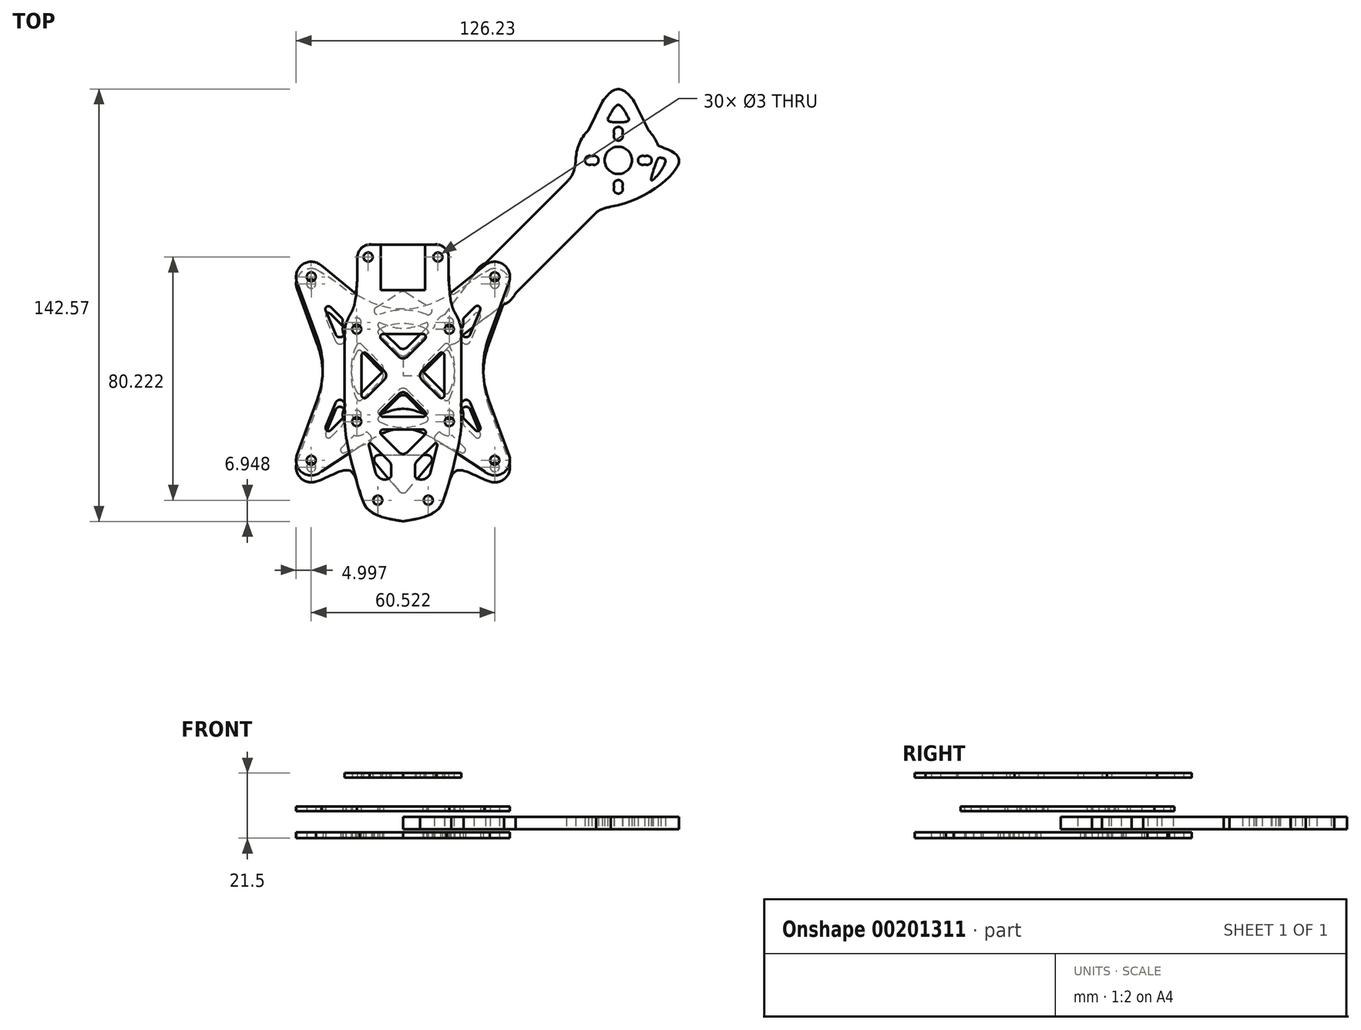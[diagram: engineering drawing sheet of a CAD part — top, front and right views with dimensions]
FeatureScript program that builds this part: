
annotation { "Feature Type Name" : "Feature", "Feature Type Description" : "" }
export const myFeature = defineFeature(function(context is Context, id is Id, definition is map)
    precondition{}
    {
        {
            var Q0;
            Q0=qCreatedBy(makeId("Top.planeOp"),FACE);
            var sketch = newSketch(context, id + "F0", { "sketchPlane" : qUnion([Q0])});
            skLineSegment(sketch, "E0.bottom", {"start": v(-15.25, 15.25) * mm, "end": v(15.25, 15.25) * mm, "construction": true});
            skLineSegment(sketch, "E0.top", {"start": v(-15.25, -15.25) * mm, "end": v(15.25, -15.25) * mm, "construction": true});
            skLineSegment(sketch, "E0.left", {"start": v(-15.25, 15.25) * mm, "end": v(-15.25, -15.25) * mm, "construction": true});
            skLineSegment(sketch, "E0.right", {"start": v(15.25, 15.25) * mm, "end": v(15.25, -15.25) * mm, "construction": true});
            skPoint(sketch, "E0.middle", {"position": v(0, 0) * mm});
            skLineSegment(sketch, "E1.bottom", {"start": v(30.25, 30.25) * mm, "end": v(-30.25, 30.25) * mm, "construction": true});
            skLineSegment(sketch, "E1.top", {"start": v(30.25, -30.25) * mm, "end": v(-30.25, -30.25) * mm, "construction": true});
            skLineSegment(sketch, "E1.left", {"start": v(30.25, 30.25) * mm, "end": v(30.25, -30.25) * mm, "construction": true});
            skLineSegment(sketch, "E1.right", {"start": v(-30.25, 30.25) * mm, "end": v(-30.25, -30.25) * mm, "construction": true});
            skLineSegment(sketch, "E2.bottom", {"start": v(-70.96, 70.96) * mm, "end": v(70.96, 70.96) * mm, "construction": true});
            skLineSegment(sketch, "E2.top", {"start": v(-70.96, -70.96) * mm, "end": v(70.96, -70.96) * mm, "construction": true});
            skLineSegment(sketch, "E2.left", {"start": v(-70.96, 70.96) * mm, "end": v(-70.96, -70.96) * mm, "construction": true});
            skLineSegment(sketch, "E2.right", {"start": v(70.96, 70.96) * mm, "end": v(70.96, -70.96) * mm, "construction": true});
            skCircle(sketch, "E3", {"center": v(70.96, 70.96) * mm, "radius": 8 * mm, "construction": true});
            skCircle(sketch, "E4", {"center": v(70.96, -70.96) * mm, "radius": 8 * mm, "construction": true});
            skCircle(sketch, "E5", {"center": v(-70.96, -70.96) * mm, "radius": 8 * mm, "construction": true});
            skCircle(sketch, "E6", {"center": v(-70.96, 70.96) * mm, "radius": 8 * mm, "construction": true});
            skCircle(sketch, "E7", {"center": v(70.96, 70.96) * mm, "radius": 9.5 * mm, "construction": true});
            skCircle(sketch, "E8", {"center": v(70.96, -70.96) * mm, "radius": 9.5 * mm, "construction": true});
            skCircle(sketch, "E9", {"center": v(-70.96, -70.96) * mm, "radius": 9.5 * mm, "construction": true});
            skCircle(sketch, "E10", {"center": v(-70.96, 70.96) * mm, "radius": 9.5 * mm, "construction": true});
            skCircle(sketch, "E11", {"center": v(70.96, 70.96) * mm, "radius": 14 * mm, "construction": true});
            skCircle(sketch, "E12", {"center": v(-70.96, 70.96) * mm, "radius": 14 * mm, "construction": true});
            skCircle(sketch, "E13", {"center": v(70.96, -70.96) * mm, "radius": 14 * mm, "construction": true});
            skCircle(sketch, "E14", {"center": v(-70.96, -70.96) * mm, "radius": 14 * mm, "construction": true});
            skCircle(sketch, "E15", {"center": v(70.96, 70.96) * mm, "radius": 63.5 * mm, "construction": true});
            skCircle(sketch, "E16", {"center": v(70.96, -70.96) * mm, "radius": 63.5 * mm, "construction": true});
            skCircle(sketch, "E17", {"center": v(-70.96, -70.96) * mm, "radius": 63.5 * mm, "construction": true});
            skCircle(sketch, "E18", {"center": v(-70.96, 70.96) * mm, "radius": 63.5 * mm, "construction": true});
            skLineSegment(sketch, "E19", {"start": v(0, 30.25) * mm, "end": v(0, 37.76) * mm, "construction": true});
            skLineSegment(sketch, "E20", {"start": v(0, 37.76) * mm, "end": v(15, 37.76) * mm, "construction": true});
            skLineSegment(sketch, "E21", {"start": v(0, -30.25) * mm, "end": v(0, -37.76) * mm, "construction": true});
            skLineSegment(sketch, "E22.bottom", {"start": v(-26.17, 26.25) * mm, "end": v(26.21, 26.25) * mm, "construction": true});
            skLineSegment(sketch, "E22.top", {"start": v(-26.21, -26.25) * mm, "end": v(26.17, -26.25) * mm, "construction": true});
            skLineSegment(sketch, "E22.left", {"start": v(-26.17, 26.25) * mm, "end": v(-26.17, -26.13) * mm, "construction": true});
            skLineSegment(sketch, "E22.right", {"start": v(26.21, 26.25) * mm, "end": v(26.21, -26.2) * mm, "construction": true});
            skCircle(sketch, "E23", {"center": v(30.25, 30.25) * mm, "radius": 5 * mm, "construction": true});
            skCircle(sketch, "E24", {"center": v(-30.25, 30.25) * mm, "radius": 5 * mm, "construction": true});
            skCircle(sketch, "E25", {"center": v(30.25, -30.25) * mm, "radius": 5 * mm, "construction": true});
            skCircle(sketch, "E26", {"center": v(-30.25, -30.25) * mm, "radius": 5 * mm, "construction": true});
            skLineSegment(sketch, "E27.bottom", {"start": v(24.5, 24.5) * mm, "end": v(-24.5, 24.5) * mm, "construction": true});
            skLineSegment(sketch, "E27.top", {"start": v(24.5, -24.5) * mm, "end": v(-24.5, -24.5) * mm, "construction": true});
            skLineSegment(sketch, "E27.left", {"start": v(24.5, 24.5) * mm, "end": v(24.5, -24.5) * mm, "construction": true});
            skLineSegment(sketch, "E27.right", {"start": v(-24.5, 24.5) * mm, "end": v(-24.5, -24.5) * mm, "construction": true});
            skLineSegment(sketch, "E28", {"start": v(-26.17, 26.25) * mm, "end": v(-30.25, 30.25) * mm, "construction": true});
            skLineSegment(sketch, "E29", {"start": v(-26.68, 26.75) * mm, "end": v(-33.82, 33.75) * mm, "construction": true});
            skLineSegment(sketch, "E30", {"start": v(-31.8, 31.77) * mm, "end": v(-28.66, 34.99) * mm, "construction": true});
            skLineSegment(sketch, "E31", {"start": v(-31.8, 31.77) * mm, "end": v(-34.96, 28.56) * mm, "construction": true});
            skArc(sketch, "E32", {"start": v(-28.66, 34.99) * mm, "mid": v(-33.82, 33.75) * mm, "end": v(-34.96, 28.56) * mm});
            skLineSegment(sketch, "E33", {"start": v(26.21, 26.25) * mm, "end": v(30.25, 30.25) * mm, "construction": true});
            skLineSegment(sketch, "E34", {"start": v(26.7, 26.73) * mm, "end": v(33.8, 33.77) * mm, "construction": true});
            skLineSegment(sketch, "E35", {"start": v(31.8, 31.78) * mm, "end": v(34.96, 28.58) * mm, "construction": true});
            skLineSegment(sketch, "E36", {"start": v(31.8, 31.78) * mm, "end": v(28.63, 34.98) * mm, "construction": true});
            skArc(sketch, "E37", {"start": v(34.96, 28.58) * mm, "mid": v(33.8, 33.77) * mm, "end": v(28.63, 34.98) * mm});
            skLineSegment(sketch, "E38", {"start": v(26.17, -26.25) * mm, "end": v(30.25, -30.25) * mm, "construction": true});
            skLineSegment(sketch, "E39", {"start": v(26.68, -26.75) * mm, "end": v(33.82, -33.75) * mm, "construction": true});
            skLineSegment(sketch, "E40", {"start": v(31.8, -31.77) * mm, "end": v(34.96, -28.56) * mm, "construction": true});
            skLineSegment(sketch, "E41", {"start": v(31.8, -31.77) * mm, "end": v(28.66, -34.99) * mm, "construction": true});
            skArc(sketch, "E42", {"start": v(28.66, -34.99) * mm, "mid": v(33.82, -33.75) * mm, "end": v(34.96, -28.56) * mm});
            skLineSegment(sketch, "E43", {"start": v(-26.21, -26.25) * mm, "end": v(-30.25, -30.25) * mm, "construction": true});
            skLineSegment(sketch, "E44", {"start": v(-26.7, -26.73) * mm, "end": v(-33.8, -33.77) * mm, "construction": true});
            skLineSegment(sketch, "E45", {"start": v(-31.8, -31.78) * mm, "end": v(-28.63, -34.98) * mm, "construction": true});
            skLineSegment(sketch, "E46", {"start": v(-31.8, -31.78) * mm, "end": v(-34.96, -28.58) * mm, "construction": true});
            skArc(sketch, "E47", {"start": v(-34.96, -28.58) * mm, "mid": v(-33.8, -33.77) * mm, "end": v(-28.63, -34.98) * mm});
            skLineSegment(sketch, "E48", {"start": v(-34.96, -28.58) * mm, "end": v(-28.28, -10.31) * mm});
            skLineSegment(sketch, "E49", {"start": v(-28.28, 10.31) * mm, "end": v(-34.96, 28.56) * mm});
            skLineSegment(sketch, "E50", {"start": v(34.96, 28.58) * mm, "end": v(28.28, 10.31) * mm});
            skLineSegment(sketch, "E51", {"start": v(28.28, -10.31) * mm, "end": v(34.96, -28.56) * mm});
            skPoint(sketch, "E52.visualSharp", {"position": v(24.5, 0) * mm});
            skArc(sketch, "E52.filletArc", {"start": v(28.28, 10.31) * mm, "mid": v(26.45, 0) * mm, "end": v(28.28, -10.31) * mm});
            skPoint(sketch, "E53.visualSharp", {"position": v(-24.5, 0) * mm});
            skArc(sketch, "E53.filletArc", {"start": v(-28.28, -10.31) * mm, "mid": v(-26.45, 0) * mm, "end": v(-28.28, 10.31) * mm});
            skFitSpline(sketch, "E54", {"points": [v(-28.66, 34.99) * mm, v(-15, 37.76) * mm], "startDerivative": vector(40.9, -21.49) * mm, "endDerivative": vector(0.75, 54.16) * mm});
            skFitSpline(sketch, "E55", {"points": [v(15, 37.76) * mm, v(28.63, 34.98) * mm], "startDerivative": vector(0.75, -54.16) * mm, "endDerivative": vector(40.9, 21.46) * mm});
            skLineSegment(sketch, "E56", {"start": v(-15.25, 19.7) * mm, "end": v(15.25, 19.7) * mm, "construction": true});
            skPoint(sketch, "E57.endSnap0", {"position": v(0, -15.25) * mm});
            skLineSegment(sketch, "E58", {"start": v(-15.25, -19.7) * mm, "end": v(15.25, -19.7) * mm, "construction": true});
            skLineSegment(sketch, "E59", {"start": v(-14.33, -37.76) * mm, "end": v(14.33, -37.76) * mm, "construction": true});
            skCircle(sketch, "E60", {"center": v(-30.25, 30.25) * mm, "radius": 1.5 * mm});
            skCircle(sketch, "E61", {"center": v(30.25, 30.25) * mm, "radius": 1.5 * mm});
            skCircle(sketch, "E62", {"center": v(15.25, 15.25) * mm, "radius": 1.5 * mm});
            skCircle(sketch, "E63", {"center": v(-15.25, 15.25) * mm, "radius": 1.5 * mm});
            skCircle(sketch, "E64", {"center": v(-15.25, -15.25) * mm, "radius": 1.5 * mm});
            skCircle(sketch, "E65", {"center": v(15.25, -15.25) * mm, "radius": 1.5 * mm});
            skCircle(sketch, "E66", {"center": v(30.25, -30.25) * mm, "radius": 1.5 * mm});
            skCircle(sketch, "E67", {"center": v(-30.25, -30.25) * mm, "radius": 1.5 * mm});
            skCircle(sketch, "E68", {"center": v(-11.5, 39.06) * mm, "radius": 1.5 * mm});
            skCircle(sketch, "E69", {"center": v(11.5, 39.06) * mm, "radius": 1.5 * mm});
            skLineSegment(sketch, "E70", {"start": v(0, 37.76) * mm, "end": v(0, 15.25) * mm, "construction": true});
            skLineSegment(sketch, "E71", {"start": v(0, -44.58) * mm, "end": v(-11, -44.58) * mm, "construction": true});
            skLineSegment(sketch, "E72", {"start": v(0, -44.58) * mm, "end": v(11, -44.58) * mm, "construction": true});
            skPoint(sketch, "E73.visualSharp", {"position": v(-14.33, -37.76) * mm});
            skPoint(sketch, "E74.visualSharp", {"position": v(14.33, -37.76) * mm});
            skCircle(sketch, "E75", {"center": v(0, 0) * mm, "radius": 17.11 * mm, "construction": true});
            skLineSegment(sketch, "E76", {"start": v(0, 0) * mm, "end": v(14.1, 14.1) * mm, "construction": true});
            skLineSegment(sketch, "E77", {"start": v(0, 0) * mm, "end": v(-15.25, 15.25) * mm, "construction": true});
            skLineSegment(sketch, "E78", {"start": v(0, 0) * mm, "end": v(-15.32, -15.32) * mm, "construction": true});
            skLineSegment(sketch, "E79", {"start": v(0, 0) * mm, "end": v(15.25, -15.25) * mm, "construction": true});
            skLineSegment(sketch, "E80", {"start": v(-10.7, 10.7) * mm, "end": v(-7.86, 13.52) * mm, "construction": true});
            skLineSegment(sketch, "E81", {"start": v(-10.7, 10.7) * mm, "end": v(-13.52, 7.86) * mm, "construction": true});
            skLineSegment(sketch, "E82", {"start": v(9.03, 9.03) * mm, "end": v(11.86, 6.2) * mm, "construction": true});
            skLineSegment(sketch, "E83", {"start": v(9.03, 9.03) * mm, "end": v(6.2, 11.86) * mm, "construction": true});
            skLineSegment(sketch, "E84", {"start": v(9.8, -9.8) * mm, "end": v(12.64, -6.98) * mm, "construction": true});
            skLineSegment(sketch, "E85", {"start": v(9.8, -9.8) * mm, "end": v(6.98, -12.64) * mm, "construction": true});
            skLineSegment(sketch, "E86", {"start": v(-9.52, -9.52) * mm, "end": v(-6.7, -12.35) * mm, "construction": true});
            skLineSegment(sketch, "E87", {"start": v(-9.52, -9.52) * mm, "end": v(-12.35, -6.7) * mm, "construction": true});
            skLineSegment(sketch, "E88.bottom", {"start": v(6.35, 6.35) * mm, "end": v(-6.35, 6.35) * mm, "construction": true});
            skLineSegment(sketch, "E88.top", {"start": v(6.35, -6.35) * mm, "end": v(-6.35, -6.35) * mm, "construction": true});
            skLineSegment(sketch, "E88.left", {"start": v(6.35, 6.35) * mm, "end": v(6.35, -6.35) * mm, "construction": true});
            skLineSegment(sketch, "E88.right", {"start": v(-6.35, 6.35) * mm, "end": v(-6.35, -6.35) * mm, "construction": true});
            skLineSegment(sketch, "E89", {"start": v(6.2, 11.86) * mm, "end": v(8.94, 14.6) * mm, "construction": true});
            skLineSegment(sketch, "E90", {"start": v(11.86, 6.2) * mm, "end": v(14.6, 8.94) * mm, "construction": true});
            skLineSegment(sketch, "E91", {"start": v(8, 13.66) * mm, "end": v(1.41, 7.07) * mm});
            skLineSegment(sketch, "E92", {"start": v(-1.41, 7.07) * mm, "end": v(-8, 13.66) * mm});
            skLineSegment(sketch, "E93", {"start": v(-13.52, 7.86) * mm, "end": v(-14.6, 8.94) * mm, "construction": true});
            skLineSegment(sketch, "E94", {"start": v(-6.7, -12.35) * mm, "end": v(-8.94, -14.6) * mm, "construction": true});
            skLineSegment(sketch, "E95", {"start": v(-8, -13.66) * mm, "end": v(-1.41, -7.07) * mm});
            skLineSegment(sketch, "E96", {"start": v(1.41, -7.07) * mm, "end": v(8, -13.66) * mm});
            skLineSegment(sketch, "E97", {"start": v(13.66, 8) * mm, "end": v(7.07, 1.41) * mm});
            skLineSegment(sketch, "E98", {"start": v(7.07, -1.41) * mm, "end": v(13.66, -8) * mm});
            skPoint(sketch, "E99", {"position": v(-7.77, 15.25) * mm});
            skPoint(sketch, "E100", {"position": v(7.77, 15.25) * mm});
            skPoint(sketch, "E101", {"position": v(15.25, 7.77) * mm});
            skPoint(sketch, "E102", {"position": v(15.25, -7.77) * mm});
            skPoint(sketch, "E103", {"position": v(7.77, -15.25) * mm});
            skPoint(sketch, "E104", {"position": v(-7.77, -15.25) * mm});
            skPoint(sketch, "E105", {"position": v(-15.25, -7.77) * mm});
            skPoint(sketch, "E106", {"position": v(-15.25, 7.77) * mm});
            skLineSegment(sketch, "E107", {"start": v(-7.79, 15.24) * mm, "end": v(-7.77, 15.25) * mm});
            skLineSegment(sketch, "E108", {"start": v(7.79, 15.24) * mm, "end": v(7.77, 15.25) * mm});
            skLineSegment(sketch, "E109", {"start": v(15.24, 7.79) * mm, "end": v(15.25, 7.77) * mm});
            skLineSegment(sketch, "E110", {"start": v(15.24, -7.79) * mm, "end": v(15.25, -7.77) * mm});
            skLineSegment(sketch, "E111", {"start": v(7.79, -15.24) * mm, "end": v(7.77, -15.25) * mm});
            skLineSegment(sketch, "E112", {"start": v(-7.77, -15.25) * mm, "end": v(-7.79, -15.24) * mm});
            skLineSegment(sketch, "E113", {"start": v(-15.24, -7.79) * mm, "end": v(-15.25, -7.77) * mm});
            skLineSegment(sketch, "E114", {"start": v(-15.24, 7.79) * mm, "end": v(-15.25, 7.77) * mm});
            skPoint(sketch, "E115", {"position": v(0, 17.11) * mm});
            skPoint(sketch, "E116", {"position": v(17.11, 0) * mm});
            skPoint(sketch, "E117", {"position": v(-17.11, 0) * mm});
            skPoint(sketch, "E118", {"position": v(0, -17.11) * mm});
            skArc(sketch, "E119", {"start": v(7.77, 15.25) * mm, "mid": v(0, 17.11) * mm, "end": v(-7.77, 15.25) * mm});
            skArc(sketch, "E120", {"start": v(15.25, -7.77) * mm, "mid": v(17.11, 0) * mm, "end": v(15.25, 7.77) * mm});
            skArc(sketch, "E121", {"start": v(-7.77, -15.25) * mm, "mid": v(0, -17.11) * mm, "end": v(7.77, -15.25) * mm});
            skArc(sketch, "E122", {"start": v(-15.25, 7.77) * mm, "mid": v(-17.11, 0) * mm, "end": v(-15.25, -7.77) * mm});
            skPoint(sketch, "E123.visualSharp", {"position": v(-5.66, 0) * mm});
            skPoint(sketch, "E124.visualSharp", {"position": v(-14.6, 8.94) * mm});
            skArc(sketch, "E124.filletArc", {"start": v(-13.66, 8) * mm, "mid": v(-14.5, 8.29) * mm, "end": v(-15.24, 7.79) * mm});
            skPoint(sketch, "E125.visualSharp", {"position": v(-14.6, -8.94) * mm});
            skArc(sketch, "E125.filletArc", {"start": v(-15.24, -7.79) * mm, "mid": v(-14.5, -8.29) * mm, "end": v(-13.66, -8) * mm});
            skPoint(sketch, "E126.visualSharp", {"position": v(-8.94, 14.6) * mm});
            skArc(sketch, "E126.filletArc", {"start": v(-7.79, 15.24) * mm, "mid": v(-8.29, 14.5) * mm, "end": v(-8, 13.66) * mm});
            skPoint(sketch, "E127.visualSharp", {"position": v(8.94, 14.6) * mm});
            skArc(sketch, "E127.filletArc", {"start": v(8, 13.66) * mm, "mid": v(8.29, 14.5) * mm, "end": v(7.79, 15.24) * mm});
            skPoint(sketch, "E128.visualSharp", {"position": v(14.6, -8.94) * mm});
            skArc(sketch, "E128.filletArc", {"start": v(13.66, -8) * mm, "mid": v(14.5, -8.29) * mm, "end": v(15.24, -7.79) * mm});
            skPoint(sketch, "E129.visualSharp", {"position": v(14.6, 8.94) * mm});
            skArc(sketch, "E129.filletArc", {"start": v(15.24, 7.79) * mm, "mid": v(14.5, 8.29) * mm, "end": v(13.66, 8) * mm});
            skPoint(sketch, "E130.visualSharp", {"position": v(8.94, -14.6) * mm});
            skArc(sketch, "E130.filletArc", {"start": v(7.79, -15.24) * mm, "mid": v(8.29, -14.5) * mm, "end": v(8, -13.66) * mm});
            skPoint(sketch, "E131.visualSharp", {"position": v(-8.94, -14.6) * mm});
            skArc(sketch, "E131.filletArc", {"start": v(-8, -13.66) * mm, "mid": v(-8.29, -14.5) * mm, "end": v(-7.79, -15.24) * mm});
            skLineSegment(sketch, "E132", {"start": v(-13.66, 8) * mm, "end": v(-7.07, 1.41) * mm});
            skLineSegment(sketch, "E133", {"start": v(-13.66, -8) * mm, "end": v(-7.07, -1.41) * mm});
            skArc(sketch, "E134.filletArc", {"start": v(-7.07, -1.41) * mm, "mid": v(-6.49, 0) * mm, "end": v(-7.07, 1.41) * mm});
            skPoint(sketch, "E135.visualSharp", {"position": v(0, -5.66) * mm});
            skArc(sketch, "E135.filletArc", {"start": v(1.41, -7.07) * mm, "mid": v(0, -6.49) * mm, "end": v(-1.41, -7.07) * mm});
            skPoint(sketch, "E136.visualSharp", {"position": v(5.66, 0) * mm});
            skArc(sketch, "E136.filletArc", {"start": v(7.07, 1.41) * mm, "mid": v(6.49, 0) * mm, "end": v(7.07, -1.41) * mm});
            skPoint(sketch, "E137.visualSharp", {"position": v(0, 5.66) * mm});
            skArc(sketch, "E137.filletArc", {"start": v(-1.41, 7.07) * mm, "mid": v(0, 6.49) * mm, "end": v(1.41, 7.07) * mm});
            skLineSegment(sketch, "E138", {"start": v(-12.9, 12.9) * mm, "end": v(-11.14, 14.67) * mm, "construction": true});
            skLineSegment(sketch, "E139", {"start": v(-12.9, 12.9) * mm, "end": v(-14.67, 11.14) * mm, "construction": true});
            skLineSegment(sketch, "E140", {"start": v(-14.67, 11.14) * mm, "end": v(-27.4, 23.87) * mm, "construction": true});
            skPoint(sketch, "E141", {"position": v(-17.57, 14.03) * mm});
            skCircle(sketch, "E142", {"center": v(-15.25, 15.25) * mm, "radius": 4.62 * mm, "construction": true});
            skLineSegment(sketch, "E143", {"start": v(-27.4, 23.87) * mm, "end": v(-21.1, 8.64) * mm, "construction": true});
            skLineSegment(sketch, "E144", {"start": v(-15.25, 15.25) * mm, "end": v(-21.32, 9.18) * mm, "construction": true});
            skLineSegment(sketch, "E145", {"start": v(-18.86, 11.64) * mm, "end": v(-19.74, 10.76) * mm});
            skLineSegment(sketch, "E146", {"start": v(-22.18, 11.25) * mm, "end": v(-25.48, 19.23) * mm});
            skLineSegment(sketch, "E147", {"start": v(-23.85, 20.32) * mm, "end": v(-20.04, 16.5) * mm});
            skLineSegment(sketch, "E148", {"start": v(-19.83, 15.85) * mm, "end": v(-19.85, 15.74) * mm});
            skLineSegment(sketch, "E149", {"start": v(-18.84, 12.33) * mm, "end": v(-18.85, 12.35) * mm});
            skPoint(sketch, "E150", {"position": v(-19.67, 13.9) * mm});
            skArc(sketch, "E151", {"start": v(-19.85, 15.74) * mm, "mid": v(-19.69, 13.95) * mm, "end": v(-18.85, 12.35) * mm});
            skPoint(sketch, "E152.visualSharp", {"position": v(-27.4, 23.87) * mm});
            skArc(sketch, "E152.filletArc", {"start": v(-23.85, 20.32) * mm, "mid": v(-25.11, 20.44) * mm, "end": v(-25.48, 19.23) * mm});
            skPoint(sketch, "E153.visualSharp", {"position": v(-21.32, 9.18) * mm});
            skArc(sketch, "E153.filletArc", {"start": v(-22.18, 11.25) * mm, "mid": v(-21.1, 10.35) * mm, "end": v(-19.74, 10.76) * mm});
            skPoint(sketch, "E154.visualSharp", {"position": v(-18.52, 11.98) * mm});
            skArc(sketch, "E154.filletArc", {"start": v(-18.86, 11.64) * mm, "mid": v(-18.7, 11.98) * mm, "end": v(-18.84, 12.33) * mm});
            skPoint(sketch, "E155.visualSharp", {"position": v(-19.77, 16.23) * mm});
            skArc(sketch, "E155.filletArc", {"start": v(-19.83, 15.85) * mm, "mid": v(-19.86, 16.2) * mm, "end": v(-20.04, 16.5) * mm});
            skCircle(sketch, "E156", {"center": v(15.23, 15.26) * mm, "radius": 4.62 * mm, "construction": true});
            skLineSegment(sketch, "E157", {"start": v(15.23, 15.26) * mm, "end": v(12.9, 12.9) * mm, "construction": true});
            skLineSegment(sketch, "E158", {"start": v(12.9, 12.9) * mm, "end": v(14.68, 11.15) * mm, "construction": true});
            skLineSegment(sketch, "E159", {"start": v(12.9, 12.9) * mm, "end": v(11.12, 14.66) * mm, "construction": true});
            skLineSegment(sketch, "E160", {"start": v(11.12, 14.66) * mm, "end": v(23.85, 27.39) * mm, "construction": true});
            skLineSegment(sketch, "E161", {"start": v(14.68, 11.15) * mm, "end": v(27.32, 23.97) * mm, "construction": true});
            skLineSegment(sketch, "E162", {"start": v(15.25, 15.25) * mm, "end": v(21.37, 9.22) * mm, "construction": true});
            skLineSegment(sketch, "E163", {"start": v(21.37, 9.22) * mm, "end": v(27.32, 23.97) * mm, "construction": true});
            skLineSegment(sketch, "E164", {"start": v(19.8, 15.9) * mm, "end": v(19.82, 15.79) * mm});
            skLineSegment(sketch, "E165", {"start": v(18.84, 12.37) * mm, "end": v(18.86, 12.4) * mm});
            skLineSegment(sketch, "E166", {"start": v(20.01, 16.55) * mm, "end": v(23.8, 20.4) * mm});
            skLineSegment(sketch, "E167", {"start": v(25.45, 19.33) * mm, "end": v(22.2, 11.3) * mm});
            skLineSegment(sketch, "E168", {"start": v(19.77, 10.8) * mm, "end": v(18.86, 11.69) * mm});
            skPoint(sketch, "E169", {"position": v(19.65, 13.92) * mm});
            skArc(sketch, "E170", {"start": v(18.86, 12.4) * mm, "mid": v(19.68, 14) * mm, "end": v(19.82, 15.79) * mm});
            skPoint(sketch, "E171.visualSharp", {"position": v(18.53, 12.02) * mm});
            skArc(sketch, "E171.filletArc", {"start": v(18.84, 12.37) * mm, "mid": v(18.72, 12.03) * mm, "end": v(18.86, 11.69) * mm});
            skPoint(sketch, "E172.visualSharp", {"position": v(19.74, 16.28) * mm});
            skArc(sketch, "E172.filletArc", {"start": v(20.01, 16.55) * mm, "mid": v(19.83, 16.25) * mm, "end": v(19.8, 15.9) * mm});
            skPoint(sketch, "E173.visualSharp", {"position": v(27.32, 23.97) * mm});
            skArc(sketch, "E173.filletArc", {"start": v(25.45, 19.33) * mm, "mid": v(25.07, 20.54) * mm, "end": v(23.8, 20.4) * mm});
            skPoint(sketch, "E174.visualSharp", {"position": v(21.37, 9.22) * mm});
            skArc(sketch, "E174.filletArc", {"start": v(19.77, 10.8) * mm, "mid": v(21.12, 10.4) * mm, "end": v(22.2, 11.3) * mm});
            skCircle(sketch, "E175", {"center": v(-15.25, -15.25) * mm, "radius": 4.62 * mm, "construction": true});
            skCircle(sketch, "E176", {"center": v(15.25, -15.25) * mm, "radius": 4.62 * mm, "construction": true});
            skLineSegment(sketch, "E177", {"start": v(-15.25, -15.25) * mm, "end": v(-12.9, -12.9) * mm, "construction": true});
            skLineSegment(sketch, "E178", {"start": v(-12.9, -12.9) * mm, "end": v(-11.14, -14.67) * mm, "construction": true});
            skLineSegment(sketch, "E179", {"start": v(-12.9, -12.9) * mm, "end": v(-14.67, -11.14) * mm, "construction": true});
            skLineSegment(sketch, "E180", {"start": v(-11.14, -14.67) * mm, "end": v(-23.87, -27.4) * mm, "construction": true});
            skLineSegment(sketch, "E181", {"start": v(-14.67, -11.14) * mm, "end": v(-27.4, -23.87) * mm, "construction": true});
            skLineSegment(sketch, "E182", {"start": v(-15.25, -15.25) * mm, "end": v(-9.18, -21.32) * mm, "construction": true});
            skLineSegment(sketch, "E183", {"start": v(-15.25, -15.25) * mm, "end": v(-21.32, -9.18) * mm, "construction": true});
            skLineSegment(sketch, "E184", {"start": v(-25.48, -19.23) * mm, "end": v(-22.18, -11.25) * mm});
            skLineSegment(sketch, "E185", {"start": v(-19.74, -10.76) * mm, "end": v(-18.86, -11.64) * mm});
            skLineSegment(sketch, "E186", {"start": v(-23.85, -20.32) * mm, "end": v(-20.04, -16.5) * mm});
            skLineSegment(sketch, "E187", {"start": v(-18.84, -12.33) * mm, "end": v(-18.85, -12.35) * mm});
            skLineSegment(sketch, "E188", {"start": v(-19.83, -15.85) * mm, "end": v(-19.85, -15.74) * mm});
            skPoint(sketch, "E189", {"position": v(-19.69, -13.94) * mm});
            skArc(sketch, "E190", {"start": v(-18.85, -12.35) * mm, "mid": v(-19.69, -13.95) * mm, "end": v(-19.85, -15.74) * mm});
            skPoint(sketch, "E191.visualSharp", {"position": v(-18.52, -11.98) * mm});
            skArc(sketch, "E191.filletArc", {"start": v(-18.84, -12.33) * mm, "mid": v(-18.7, -11.98) * mm, "end": v(-18.86, -11.64) * mm});
            skPoint(sketch, "E192.visualSharp", {"position": v(-19.77, -16.23) * mm});
            skArc(sketch, "E192.filletArc", {"start": v(-20.04, -16.5) * mm, "mid": v(-19.86, -16.2) * mm, "end": v(-19.83, -15.85) * mm});
            skPoint(sketch, "E193.visualSharp", {"position": v(-27.4, -23.87) * mm});
            skArc(sketch, "E193.filletArc", {"start": v(-25.48, -19.23) * mm, "mid": v(-25.11, -20.44) * mm, "end": v(-23.85, -20.32) * mm});
            skPoint(sketch, "E194.visualSharp", {"position": v(-21.32, -9.18) * mm});
            skArc(sketch, "E194.filletArc", {"start": v(-19.74, -10.76) * mm, "mid": v(-21.1, -10.35) * mm, "end": v(-22.18, -11.25) * mm});
            skLineSegment(sketch, "E195", {"start": v(15.25, -15.25) * mm, "end": v(12.9, -12.9) * mm, "construction": true});
            skLineSegment(sketch, "E196", {"start": v(12.9, -12.9) * mm, "end": v(14.67, -11.14) * mm, "construction": true});
            skLineSegment(sketch, "E197", {"start": v(12.9, -12.9) * mm, "end": v(11.14, -14.67) * mm, "construction": true});
            skLineSegment(sketch, "E198", {"start": v(14.67, -11.14) * mm, "end": v(27.4, -23.87) * mm, "construction": true});
            skLineSegment(sketch, "E199", {"start": v(15.25, -15.25) * mm, "end": v(21.32, -9.18) * mm, "construction": true});
            skLineSegment(sketch, "E200", {"start": v(22.18, -11.25) * mm, "end": v(25.48, -19.23) * mm});
            skLineSegment(sketch, "E201", {"start": v(23.85, -20.32) * mm, "end": v(20.04, -16.5) * mm});
            skLineSegment(sketch, "E202", {"start": v(19.74, -10.76) * mm, "end": v(18.86, -11.64) * mm});
            skLineSegment(sketch, "E203", {"start": v(18.84, -12.33) * mm, "end": v(18.85, -12.35) * mm});
            skLineSegment(sketch, "E204", {"start": v(19.83, -15.85) * mm, "end": v(19.85, -15.74) * mm});
            skPoint(sketch, "E205", {"position": v(19.64, -13.8) * mm});
            skArc(sketch, "E206", {"start": v(19.85, -15.74) * mm, "mid": v(19.69, -13.95) * mm, "end": v(18.85, -12.35) * mm});
            skPoint(sketch, "E207.visualSharp", {"position": v(21.32, -9.18) * mm});
            skArc(sketch, "E207.filletArc", {"start": v(22.18, -11.25) * mm, "mid": v(21.1, -10.35) * mm, "end": v(19.74, -10.76) * mm});
            skPoint(sketch, "E208.visualSharp", {"position": v(19.77, -16.23) * mm});
            skArc(sketch, "E208.filletArc", {"start": v(19.83, -15.85) * mm, "mid": v(19.86, -16.2) * mm, "end": v(20.04, -16.5) * mm});
            skPoint(sketch, "E209.visualSharp", {"position": v(18.52, -11.98) * mm});
            skArc(sketch, "E209.filletArc", {"start": v(18.86, -11.64) * mm, "mid": v(18.7, -11.98) * mm, "end": v(18.84, -12.33) * mm});
            skPoint(sketch, "E210.visualSharp", {"position": v(27.4, -23.87) * mm});
            skArc(sketch, "E210.filletArc", {"start": v(23.85, -20.32) * mm, "mid": v(25.11, -20.44) * mm, "end": v(25.48, -19.23) * mm});
            skPoint(sketch, "E211", {"position": v(0, -48.1) * mm});
            skLineSegment(sketch, "E212", {"start": v(0, -31.42) * mm, "end": v(17.54, -31.42) * mm, "construction": true});
            skLineSegment(sketch, "E213", {"start": v(0, -31.42) * mm, "end": v(-17.54, -31.42) * mm, "construction": true});
            skFitSpline(sketch, "E214", {"points": [v(28.66, -34.99) * mm, v(17.54, -31.42) * mm, v(14.33, -37.76) * mm], "startDerivative": vector(-22.15, 6.9) * mm, "endDerivative": vector(-5.52, -13.66) * mm});
            skFitSpline(sketch, "E215", {"points": [v(14.33, -37.76) * mm, v(11, -44.58) * mm, v(0, -48.1) * mm], "startDerivative": vector(-4.65, -17.21) * mm, "endDerivative": vector(-23.36, -3.95) * mm});
            skFitSpline(sketch, "E216", {"points": [v(-28.63, -34.98) * mm, v(-17.54, -31.42) * mm, v(-14.33, -37.76) * mm], "startDerivative": vector(22.11, 6.89) * mm, "endDerivative": vector(5.52, -13.65) * mm});
            skFitSpline(sketch, "E217", {"points": [v(-14.33, -37.76) * mm, v(-11, -44.58) * mm, v(0, -48.1) * mm], "startDerivative": vector(4.65, -17.21) * mm, "endDerivative": vector(23.36, -3.95) * mm});
            skLineSegment(sketch, "E218", {"start": v(-19.23, -25.48) * mm, "end": v(-11.25, -22.18) * mm});
            skLineSegment(sketch, "E219", {"start": v(-10.76, -19.74) * mm, "end": v(-11.64, -18.86) * mm});
            skLineSegment(sketch, "E220", {"start": v(-12.33, -18.84) * mm, "end": v(-12.35, -18.85) * mm});
            skLineSegment(sketch, "E221", {"start": v(-20.32, -23.85) * mm, "end": v(-16.5, -20.04) * mm});
            skLineSegment(sketch, "E222", {"start": v(-15.85, -19.83) * mm, "end": v(-15.74, -19.85) * mm});
            skPoint(sketch, "E223.visualSharp", {"position": v(-9.18, -21.32) * mm});
            skArc(sketch, "E223.filletArc", {"start": v(-11.25, -22.18) * mm, "mid": v(-10.35, -21.1) * mm, "end": v(-10.76, -19.74) * mm});
            skPoint(sketch, "E224.visualSharp", {"position": v(-11.98, -18.52) * mm});
            skArc(sketch, "E224.filletArc", {"start": v(-11.64, -18.86) * mm, "mid": v(-11.98, -18.7) * mm, "end": v(-12.33, -18.84) * mm});
            skPoint(sketch, "E225.visualSharp", {"position": v(-16.23, -19.77) * mm});
            skArc(sketch, "E225.filletArc", {"start": v(-15.85, -19.83) * mm, "mid": v(-16.2, -19.86) * mm, "end": v(-16.5, -20.04) * mm});
            skPoint(sketch, "E226.visualSharp", {"position": v(-23.87, -27.4) * mm});
            skArc(sketch, "E226.filletArc", {"start": v(-20.32, -23.85) * mm, "mid": v(-20.44, -25.11) * mm, "end": v(-19.23, -25.48) * mm});
            skLineSegment(sketch, "E227", {"start": v(15.25, -15.25) * mm, "end": v(9.18, -21.32) * mm, "construction": true});
            skLineSegment(sketch, "E228", {"start": v(11.14, -14.67) * mm, "end": v(23.87, -27.4) * mm, "construction": true});
            skLineSegment(sketch, "E229", {"start": v(19.23, -25.48) * mm, "end": v(11.25, -22.18) * mm});
            skLineSegment(sketch, "E230", {"start": v(10.76, -19.74) * mm, "end": v(11.64, -18.86) * mm});
            skLineSegment(sketch, "E231", {"start": v(12.33, -18.84) * mm, "end": v(12.35, -18.85) * mm});
            skLineSegment(sketch, "E232", {"start": v(20.32, -23.85) * mm, "end": v(16.5, -20.04) * mm});
            skLineSegment(sketch, "E233", {"start": v(15.85, -19.83) * mm, "end": v(15.74, -19.85) * mm});
            skPoint(sketch, "E234", {"position": v(13.76, -19.63) * mm});
            skArc(sketch, "E235", {"start": v(12.35, -18.85) * mm, "mid": v(13.95, -19.69) * mm, "end": v(15.74, -19.85) * mm});
            skPoint(sketch, "E236.visualSharp", {"position": v(9.18, -21.32) * mm});
            skArc(sketch, "E236.filletArc", {"start": v(10.76, -19.74) * mm, "mid": v(10.35, -21.1) * mm, "end": v(11.25, -22.18) * mm});
            skPoint(sketch, "E237.visualSharp", {"position": v(11.98, -18.52) * mm});
            skArc(sketch, "E237.filletArc", {"start": v(12.33, -18.84) * mm, "mid": v(11.98, -18.7) * mm, "end": v(11.64, -18.86) * mm});
            skPoint(sketch, "E238.visualSharp", {"position": v(23.87, -27.4) * mm});
            skArc(sketch, "E238.filletArc", {"start": v(19.23, -25.48) * mm, "mid": v(20.44, -25.11) * mm, "end": v(20.32, -23.85) * mm});
            skPoint(sketch, "E239.visualSharp", {"position": v(16.23, -19.77) * mm});
            skArc(sketch, "E239.filletArc", {"start": v(16.5, -20.04) * mm, "mid": v(16.2, -19.86) * mm, "end": v(15.85, -19.83) * mm});
            skPoint(sketch, "E240", {"position": v(-14.29, -19.77) * mm});
            skArc(sketch, "E241", {"start": v(-15.74, -19.85) * mm, "mid": v(-13.95, -19.69) * mm, "end": v(-12.35, -18.85) * mm});
            skLineSegment(sketch, "E242", {"start": v(-13.27, -41.16) * mm, "end": v(-8.27, -41.16) * mm, "construction": true});
            skLineSegment(sketch, "E243", {"start": v(-8.27, -41.16) * mm, "end": v(-8.27, -46.16) * mm, "construction": true});
            skLineSegment(sketch, "E244", {"start": v(13.27, -41.16) * mm, "end": v(8.27, -41.16) * mm, "construction": true});
            skLineSegment(sketch, "E245", {"start": v(8.27, -41.16) * mm, "end": v(8.27, -46.16) * mm, "construction": true});
            skCircle(sketch, "E246", {"center": v(8.27, -41.16) * mm, "radius": 1.5 * mm});
            skCircle(sketch, "E247", {"center": v(-8.27, -41.16) * mm, "radius": 1.5 * mm});
            skLineSegment(sketch, "E248", {"start": v(-8.94, 14.6) * mm, "end": v(-8.94, 19.63) * mm, "construction": true});
            skLineSegment(sketch, "E249", {"start": v(8.94, 14.6) * mm, "end": v(8.94, 19.63) * mm, "construction": true});
            skPoint(sketch, "E250", {"position": v(0, 21.57) * mm});
            skLineSegment(sketch, "E251", {"start": v(-7.77, 15.25) * mm, "end": v(-7.77, 20.12) * mm, "construction": true});
            skLineSegment(sketch, "E252", {"start": v(7.79, 15.24) * mm, "end": v(7.79, 20.11) * mm, "construction": true});
            skLineSegment(sketch, "E253", {"start": v(-8.94, 19.63) * mm, "end": v(-8.94, 22.43) * mm, "construction": true});
            skLineSegment(sketch, "E254", {"start": v(8.94, 19.63) * mm, "end": v(8.94, 22.43) * mm, "construction": true});
            skLineSegment(sketch, "E255", {"start": v(-8.94, 22.43) * mm, "end": v(-1.06, 27.36) * mm});
            skLineSegment(sketch, "E256", {"start": v(1.06, 27.36) * mm, "end": v(8.94, 22.43) * mm});
            skArc(sketch, "E257", {"start": v(-8.94, 22.43) * mm, "mid": v(-9.4, 20.74) * mm, "end": v(-7.77, 20.12) * mm});
            skArc(sketch, "E258", {"start": v(7.79, 20.11) * mm, "mid": v(9.41, 20.75) * mm, "end": v(8.94, 22.43) * mm});
            skPoint(sketch, "E259.visualSharp", {"position": v(0, 28.02) * mm});
            skArc(sketch, "E259.filletArc", {"start": v(1.06, 27.36) * mm, "mid": v(0, 27.66) * mm, "end": v(-1.06, 27.36) * mm});
            skArc(sketch, "E260", {"start": v(7.79, 20.11) * mm, "mid": v(0, 21.57) * mm, "end": v(-7.77, 20.12) * mm});
            skLineSegment(sketch, "E261", {"start": v(-8.94, -14.6) * mm, "end": v(-8.94, -19.63) * mm, "construction": true});
            skLineSegment(sketch, "E262", {"start": v(-7.77, -15.25) * mm, "end": v(-7.77, -20.12) * mm, "construction": true});
            skLineSegment(sketch, "E263", {"start": v(7.79, -15.24) * mm, "end": v(7.79, -20.11) * mm, "construction": true});
            skLineSegment(sketch, "E264", {"start": v(8.94, -14.6) * mm, "end": v(8.94, -19.63) * mm, "construction": true});
            skLineSegment(sketch, "E265", {"start": v(-8.94, -19.63) * mm, "end": v(-8.94, -22.43) * mm, "construction": true});
            skLineSegment(sketch, "E266", {"start": v(8.94, -19.63) * mm, "end": v(8.94, -22.43) * mm, "construction": true});
            skPoint(sketch, "E267", {"position": v(0, -26.25) * mm});
            skPoint(sketch, "E268.visualSharp", {"position": v(0, -30.25) * mm});
            skPoint(sketch, "E269", {"position": v(0, -24.5) * mm});
            skLineSegment(sketch, "E270", {"start": v(0, -26.25) * mm, "end": v(-11.25, -26.25) * mm, "construction": true});
            skLineSegment(sketch, "E271", {"start": v(0, -26.25) * mm, "end": v(11.25, -26.25) * mm, "construction": true});
            skPoint(sketch, "E272.visualSharp", {"position": v(-11.25, -26.25) * mm});
            skPoint(sketch, "E273.visualSharp", {"position": v(11.25, -26.25) * mm});
            skPoint(sketch, "E274.visualSharp", {"position": v(0, -37.76) * mm});
            skPoint(sketch, "E275", {"position": v(0, -39.7) * mm});
            skLineSegment(sketch, "E276", {"start": v(-9.19, -28.72) * mm, "end": v(-1.34, -38.1) * mm});
            skLineSegment(sketch, "E277", {"start": v(1.34, -38.1) * mm, "end": v(9.19, -28.72) * mm});
            skLineSegment(sketch, "E278", {"start": v(-8.04, -26.25) * mm, "end": v(8.04, -26.25) * mm});
            skArc(sketch, "E279.filletArc", {"start": v(-8.04, -26.25) * mm, "mid": v(-9.4, -27.12) * mm, "end": v(-9.19, -28.72) * mm});
            skArc(sketch, "E280.filletArc", {"start": v(9.19, -28.72) * mm, "mid": v(9.4, -27.12) * mm, "end": v(8.04, -26.25) * mm});
            skArc(sketch, "E281.filletArc", {"start": v(-1.34, -38.1) * mm, "mid": v(0, -38.72) * mm, "end": v(1.34, -38.1) * mm});
            skLineSegment(sketch, "E282", {"start": v(0, 34) * mm, "end": v(8.73, 34) * mm, "construction": true});
            skLineSegment(sketch, "E283", {"start": v(0, 34) * mm, "end": v(-8.73, 34) * mm, "construction": true});
            skLineSegment(sketch, "E284", {"start": v(-11.5, 39.06) * mm, "end": v(0, 39.06) * mm, "construction": true});
            skLineSegment(sketch, "E285", {"start": v(0, 39.06) * mm, "end": v(11.5, 39.06) * mm, "construction": true});
            skLineSegment(sketch, "E286", {"start": v(-11.5, 39.06) * mm, "end": v(-15.5, 39.06) * mm, "construction": true});
            skLineSegment(sketch, "E287", {"start": v(11.5, 39.06) * mm, "end": v(11.5, 26.25) * mm, "construction": true});
            skLineSegment(sketch, "E288", {"start": v(0, 43.2) * mm, "end": v(-10.44, 43.2) * mm});
            skLineSegment(sketch, "E289", {"start": v(0, 43.2) * mm, "end": v(10.44, 43.2) * mm});
            skLineSegment(sketch, "E290", {"start": v(-15.03, 35.79) * mm, "end": v(-11.5, 43.2) * mm, "construction": true});
            skPoint(sketch, "E291.visualSharp", {"position": v(-11.5, 43.2) * mm});
            skPoint(sketch, "E292.visualSharp", {"position": v(11.5, 43.2) * mm});
            skLineSegment(sketch, "E293", {"start": v(-15.03, 35.79) * mm, "end": v(-15, 39.06) * mm});
            skLineSegment(sketch, "E294", {"start": v(15.03, 35.79) * mm, "end": v(15.03, 39.06) * mm});
            skArc(sketch, "E295", {"start": v(-10.44, 43.2) * mm, "mid": v(-13.62, 42.13) * mm, "end": v(-15, 39.06) * mm});
            skArc(sketch, "E296", {"start": v(15.03, 39.06) * mm, "mid": v(13.65, 42.15) * mm, "end": v(10.44, 43.2) * mm});
            skSolve(sketch);
        }
        {
            var Q0;
            Q0=qCreatedBy(makeId("Top.planeOp"),FACE);
            var sketch = newSketch(context, id + "F1", { "sketchPlane" : qUnion([Q0])});
            skLineSegment(sketch, "E297.bottom", {"start": v(-15.24, 15.25) * mm, "end": v(15.26, 15.25) * mm, "construction": true});
            skLineSegment(sketch, "E297.top", {"start": v(-15.24, -15.25) * mm, "end": v(15.26, -15.25) * mm, "construction": true});
            skLineSegment(sketch, "E297.left", {"start": v(-15.24, 15.25) * mm, "end": v(-15.24, -15.25) * mm, "construction": true});
            skLineSegment(sketch, "E297.right", {"start": v(15.26, 15.25) * mm, "end": v(15.26, -15.25) * mm, "construction": true});
            skPoint(sketch, "E297.middle", {"position": v(0, 0) * mm});
            skLineSegment(sketch, "E298.bottom", {"start": v(30.26, 30.25) * mm, "end": v(-30.24, 30.25) * mm, "construction": true});
            skLineSegment(sketch, "E298.top", {"start": v(30.26, -30.25) * mm, "end": v(-30.24, -30.25) * mm, "construction": true});
            skLineSegment(sketch, "E298.left", {"start": v(30.26, 30.25) * mm, "end": v(30.26, -30.25) * mm, "construction": true});
            skLineSegment(sketch, "E298.right", {"start": v(-30.24, 30.25) * mm, "end": v(-30.24, -30.25) * mm, "construction": true});
            skLineSegment(sketch, "E299.bottom", {"start": v(-70.95, 70.96) * mm, "end": v(70.97, 70.96) * mm, "construction": true});
            skLineSegment(sketch, "E299.top", {"start": v(-70.95, -70.96) * mm, "end": v(70.97, -70.96) * mm, "construction": true});
            skLineSegment(sketch, "E299.left", {"start": v(-70.95, 70.96) * mm, "end": v(-70.95, -70.96) * mm, "construction": true});
            skLineSegment(sketch, "E299.right", {"start": v(70.97, 70.96) * mm, "end": v(70.97, -70.96) * mm, "construction": true});
            skCircle(sketch, "E300", {"center": v(70.97, 70.96) * mm, "radius": 4.5 * mm});
            skCircle(sketch, "E301", {"center": v(-70.95, 70.96) * mm, "radius": 4.5 * mm, "construction": true});
            skCircle(sketch, "E302", {"center": v(70.97, -70.96) * mm, "radius": 4.5 * mm, "construction": true});
            skCircle(sketch, "E303", {"center": v(-70.95, -70.96) * mm, "radius": 4.5 * mm, "construction": true});
            skCircle(sketch, "E304", {"center": v(70.97, 70.96) * mm, "radius": 8 * mm, "construction": true});
            skCircle(sketch, "E305", {"center": v(70.97, -70.96) * mm, "radius": 8 * mm, "construction": true});
            skCircle(sketch, "E306", {"center": v(-70.95, -70.96) * mm, "radius": 8 * mm, "construction": true});
            skCircle(sketch, "E307", {"center": v(-70.95, 70.96) * mm, "radius": 8 * mm, "construction": true});
            skCircle(sketch, "E308", {"center": v(70.97, 70.96) * mm, "radius": 9.5 * mm, "construction": true});
            skCircle(sketch, "E309", {"center": v(70.97, -70.96) * mm, "radius": 9.5 * mm, "construction": true});
            skCircle(sketch, "E310", {"center": v(-70.95, -70.96) * mm, "radius": 9.5 * mm, "construction": true});
            skCircle(sketch, "E311", {"center": v(-70.95, 70.96) * mm, "radius": 9.5 * mm, "construction": true});
            skCircle(sketch, "E312", {"center": v(70.97, 70.96) * mm, "radius": 14 * mm, "construction": true});
            skCircle(sketch, "E313", {"center": v(-70.95, 70.96) * mm, "radius": 14 * mm, "construction": true});
            skCircle(sketch, "E314", {"center": v(70.97, -70.96) * mm, "radius": 14 * mm, "construction": true});
            skCircle(sketch, "E315", {"center": v(-70.95, -70.96) * mm, "radius": 14 * mm, "construction": true});
            skCircle(sketch, "E316", {"center": v(70.97, 70.96) * mm, "radius": 63.5 * mm, "construction": true});
            skCircle(sketch, "E317", {"center": v(70.97, -70.96) * mm, "radius": 63.5 * mm, "construction": true});
            skCircle(sketch, "E318", {"center": v(-70.95, -70.96) * mm, "radius": 63.5 * mm, "construction": true});
            skCircle(sketch, "E319", {"center": v(-70.95, 70.96) * mm, "radius": 63.5 * mm, "construction": true});
            skLineSegment(sketch, "E320", {"start": v(0, 30.25) * mm, "end": v(0, 36.4) * mm, "construction": true});
            skLineSegment(sketch, "E321", {"start": v(0, 36.4) * mm, "end": v(-14.28, 36.4) * mm, "construction": true});
            skLineSegment(sketch, "E322", {"start": v(0, 36.4) * mm, "end": v(14.3, 36.4) * mm, "construction": true});
            skLineSegment(sketch, "E323", {"start": v(0, -30.25) * mm, "end": v(0, -36.4) * mm, "construction": true});
            skLineSegment(sketch, "E324", {"start": v(0, -36.4) * mm, "end": v(-14.28, -36.4) * mm, "construction": true});
            skLineSegment(sketch, "E325", {"start": v(0, -36.4) * mm, "end": v(14.3, -36.4) * mm, "construction": true});
            skLineSegment(sketch, "E326.bottom", {"start": v(-26.18, 26.2) * mm, "end": v(26.2, 26.2) * mm, "construction": true});
            skLineSegment(sketch, "E326.top", {"start": v(-26.18, -26.19) * mm, "end": v(26.2, -26.19) * mm, "construction": true});
            skLineSegment(sketch, "E326.left", {"start": v(-26.18, 26.2) * mm, "end": v(-26.18, -26.19) * mm, "construction": true});
            skLineSegment(sketch, "E326.right", {"start": v(26.2, 26.2) * mm, "end": v(26.2, -26.19) * mm, "construction": true});
            skCircle(sketch, "E327", {"center": v(30.26, 30.25) * mm, "radius": 7.5 * mm, "construction": true});
            skCircle(sketch, "E328", {"center": v(-30.24, 30.25) * mm, "radius": 7.5 * mm, "construction": true});
            skCircle(sketch, "E329", {"center": v(30.26, -30.25) * mm, "radius": 7.5 * mm, "construction": true});
            skCircle(sketch, "E330", {"center": v(-30.24, -30.25) * mm, "radius": 7.5 * mm, "construction": true});
            skCircle(sketch, "E331", {"center": v(15.26, 15.25) * mm, "radius": 1.5 * mm, "construction": true});
            skCircle(sketch, "E332", {"center": v(-15.24, 15.25) * mm, "radius": 1.5 * mm, "construction": true});
            skCircle(sketch, "E333", {"center": v(15.26, -15.25) * mm, "radius": 1.5 * mm, "construction": true});
            skCircle(sketch, "E334", {"center": v(-15.24, -15.25) * mm, "radius": 1.5 * mm, "construction": true});
            skLineSegment(sketch, "E335", {"start": v(15.26, 15.25) * mm, "end": v(0, 0) * mm, "construction": true});
            skLineSegment(sketch, "E336", {"start": v(-15.24, 15.25) * mm, "end": v(0, 0) * mm, "construction": true});
            skLineSegment(sketch, "E337", {"start": v(15.26, -15.25) * mm, "end": v(0, 0) * mm, "construction": true});
            skLineSegment(sketch, "E338", {"start": v(-15.24, -15.25) * mm, "end": v(0, 0) * mm, "construction": true});
            skCircle(sketch, "E339", {"center": v(15.26, 15.25) * mm, "radius": 5 * mm, "construction": true});
            skCircle(sketch, "E340", {"center": v(-15.24, 15.25) * mm, "radius": 5 * mm, "construction": true});
            skCircle(sketch, "E341", {"center": v(-15.24, -15.25) * mm, "radius": 5 * mm, "construction": true});
            skCircle(sketch, "E342", {"center": v(15.26, -15.25) * mm, "radius": 5 * mm, "construction": true});
            skLineSegment(sketch, "E343.bottom", {"start": v(-5.65, -5.65) * mm, "end": v(5.66, -5.65) * mm, "construction": true});
            skLineSegment(sketch, "E343.top", {"start": v(-5.65, 5.66) * mm, "end": v(5.66, 5.66) * mm, "construction": true});
            skLineSegment(sketch, "E343.left", {"start": v(-5.65, -5.65) * mm, "end": v(-5.65, 5.66) * mm, "construction": true});
            skLineSegment(sketch, "E343.right", {"start": v(5.66, -5.65) * mm, "end": v(5.66, 5.66) * mm, "construction": true});
            skPoint(sketch, "E344", {"position": v(0, 5.66) * mm});
            skPoint(sketch, "E345", {"position": v(5.66, 0) * mm});
            skPoint(sketch, "E346", {"position": v(-5.65, 0) * mm});
            skPoint(sketch, "E347", {"position": v(0, -5.65) * mm});
            skLineSegment(sketch, "E348", {"start": v(15.26, 15.25) * mm, "end": v(70.97, 70.96) * mm, "construction": true});
            skLineSegment(sketch, "E349", {"start": v(61.07, 61.06) * mm, "end": v(56.12, 66.01) * mm, "construction": true});
            skLineSegment(sketch, "E350", {"start": v(61.07, 61.06) * mm, "end": v(66.02, 56.11) * mm, "construction": true});
            skCircle(sketch, "E351", {"center": v(70.97, 70.96) * mm, "radius": 23.5 * mm, "construction": true});
            skLineSegment(sketch, "E352", {"start": v(70.97, 70.96) * mm, "end": v(70.97, 94.46) * mm, "construction": true});
            skLineSegment(sketch, "E353", {"start": v(70.97, 70.96) * mm, "end": v(94.47, 70.96) * mm, "construction": true});
            skLineSegment(sketch, "E354", {"start": v(53.84, 63.73) * mm, "end": v(27.21, 37.1) * mm});
            skLineSegment(sketch, "E355", {"start": v(63.66, 53.75) * mm, "end": v(37.11, 27.2) * mm});
            skCircle(sketch, "E356", {"center": v(70.97, 70.96) * mm, "radius": 15.5 * mm, "construction": true});
            skLineSegment(sketch, "E357", {"start": v(70.97, 70.96) * mm, "end": v(54.35, 87.58) * mm, "construction": true});
            skLineSegment(sketch, "E358", {"start": v(70.97, 70.96) * mm, "end": v(87.59, 54.34) * mm, "construction": true});
            skLineSegment(sketch, "E359", {"start": v(70.97, 70.96) * mm, "end": v(87.59, 87.58) * mm, "construction": true});
            skLineSegment(sketch, "E360", {"start": v(87.59, 54.34) * mm, "end": v(93, 62.76) * mm, "construction": true});
            skLineSegment(sketch, "E361", {"start": v(87.59, 87.58) * mm, "end": v(90.73, 83.69) * mm, "construction": true});
            skLineSegment(sketch, "E362", {"start": v(87.59, 87.58) * mm, "end": v(83.7, 90.72) * mm, "construction": true});
            skLineSegment(sketch, "E363", {"start": v(54.35, 87.58) * mm, "end": v(62.77, 92.98) * mm, "construction": true});
            skCircle(sketch, "E364", {"center": v(70.97, 70.96) * mm, "radius": 20 * mm, "construction": true});
            skLineSegment(sketch, "E365", {"start": v(62.77, 92.98) * mm, "end": v(64.71, 89.96) * mm, "construction": true});
            skLineSegment(sketch, "E366", {"start": v(83.7, 90.72) * mm, "end": v(81.48, 87.97) * mm, "construction": true});
            skLineSegment(sketch, "E367", {"start": v(90.73, 83.69) * mm, "end": v(87.98, 81.47) * mm, "construction": true});
            skPoint(sketch, "E368", {"position": v(56.83, 85.1) * mm});
            skPoint(sketch, "E369", {"position": v(58.56, 90.28) * mm});
            skLineSegment(sketch, "E370", {"start": v(64.71, 89.96) * mm, "end": v(81.48, 87.97) * mm, "construction": true});
            skLineSegment(sketch, "E371", {"start": v(73.1, 88.96) * mm, "end": v(72.79, 86.35) * mm, "construction": true});
            skLineSegment(sketch, "E372", {"start": v(72.79, 86.35) * mm, "end": v(72.61, 84.86) * mm, "construction": true});
            skPoint(sketch, "E373", {"position": v(90.29, 58.55) * mm});
            skLineSegment(sketch, "E374", {"start": v(93, 62.76) * mm, "end": v(89.96, 64.7) * mm, "construction": true});
            skPoint(sketch, "E375", {"position": v(85.11, 56.82) * mm});
            skPoint(sketch, "E376.visualSharp", {"position": v(56.97, 70.96) * mm});
            skPoint(sketch, "E377.visualSharp", {"position": v(72.61, 84.86) * mm});
            skPoint(sketch, "E378.visualSharp", {"position": v(84.97, 70.96) * mm});
            skPoint(sketch, "E379.visualSharp", {"position": v(70.97, 56.84) * mm});
            skPoint(sketch, "E380.visualSharp", {"position": v(56.12, 66.01) * mm});
            skPoint(sketch, "E381.visualSharp", {"position": v(66.02, 56.11) * mm});
            skLineSegment(sketch, "E382", {"start": v(76.63, 76.62) * mm, "end": v(79.8, 79.8) * mm, "construction": true});
            skLineSegment(sketch, "E383", {"start": v(70.97, 90.26) * mm, "end": v(65.72, 90.26) * mm, "construction": true});
            skLineSegment(sketch, "E384", {"start": v(70.97, 90.26) * mm, "end": v(76.22, 90.26) * mm, "construction": true});
            skFitSpline(sketch, "E385", {"points": [v(65.72, 90.26) * mm, v(70.97, 94.46) * mm, v(76.22, 90.26) * mm], "startDerivative": vector(9, 14.06) * mm, "endDerivative": vector(9, -14.06) * mm});
            skLineSegment(sketch, "E386", {"start": v(70.97, 92.6) * mm, "end": v(74.72, 92.6) * mm, "construction": true});
            skLineSegment(sketch, "E387", {"start": v(70.97, 92.6) * mm, "end": v(67.22, 92.6) * mm, "construction": true});
            skLineSegment(sketch, "E388", {"start": v(65.72, 90.26) * mm, "end": v(61.07, 80.86) * mm});
            skPoint(sketch, "E389", {"position": v(57.94, 76.1) * mm});
            skArc(sketch, "E390", {"start": v(61.07, 80.86) * mm, "mid": v(58.04, 76.32) * mm, "end": v(56.97, 70.96) * mm});
            skPoint(sketch, "E391", {"position": v(84.09, 75.85) * mm});
            skFitSpline(sketch, "E392", {"points": [v(84.09, 75.85) * mm, v(90.97, 70.96) * mm, v(68.49, 55.66) * mm], "startDerivative": vector(24.48, -10.1) * mm, "endDerivative": vector(-49.92, -7.72) * mm});
            skFitSpline(sketch, "E393", {"points": [v(53.84, 63.73) * mm, v(56.97, 70.96) * mm], "startDerivative": vector(4.73, 4.42) * mm, "endDerivative": vector(1.47, 12.68) * mm});
            skLineSegment(sketch, "E394", {"start": v(16.8, 16.8) * mm, "end": v(13.62, 19.97) * mm, "construction": true});
            skLineSegment(sketch, "E395", {"start": v(16.8, 16.8) * mm, "end": v(19.98, 13.6) * mm, "construction": true});
            skLineSegment(sketch, "E396", {"start": v(37.11, 27.2) * mm, "end": v(33.3, 23.4) * mm, "construction": true});
            skLineSegment(sketch, "E397", {"start": v(27.21, 37.1) * mm, "end": v(23.4, 33.3) * mm, "construction": true});
            skLineSegment(sketch, "E398", {"start": v(23.4, 33.3) * mm, "end": v(13.62, 19.97) * mm});
            skLineSegment(sketch, "E399", {"start": v(33.3, 23.4) * mm, "end": v(19.98, 13.6) * mm});
            skPoint(sketch, "E400", {"position": v(25.01, 35.61) * mm});
            skPoint(sketch, "E401", {"position": v(35.69, 25.07) * mm});
            skArc(sketch, "E402", {"start": v(33.3, 23.4) * mm, "mid": v(35.56, 24.95) * mm, "end": v(37.11, 27.2) * mm});
            skArc(sketch, "E403", {"start": v(27.21, 37.1) * mm, "mid": v(24.96, 35.55) * mm, "end": v(23.4, 33.3) * mm});
            skLineSegment(sketch, "E404.bottom", {"start": v(0, 5.66) * mm, "end": v(6.37, 5.66) * mm, "construction": true});
            skLineSegment(sketch, "E404.top", {"start": v(0, 12.02) * mm, "end": v(6.37, 12.02) * mm, "construction": true});
            skLineSegment(sketch, "E404.left", {"start": v(0, 5.66) * mm, "end": v(0, 12.02) * mm, "construction": true});
            skLineSegment(sketch, "E404.right", {"start": v(6.37, 5.66) * mm, "end": v(6.37, 12.02) * mm, "construction": true});
            skLineSegment(sketch, "E405", {"start": v(0, 5.66) * mm, "end": v(6.37, 12.02) * mm});
            skLineSegment(sketch, "E406", {"start": v(6.37, 12.02) * mm, "end": v(10.3, 15.95) * mm});
            skLineSegment(sketch, "E407.bottom", {"start": v(5.66, 0) * mm, "end": v(12.02, 0) * mm, "construction": true});
            skLineSegment(sketch, "E407.top", {"start": v(5.66, 6.36) * mm, "end": v(12.02, 6.36) * mm, "construction": true});
            skLineSegment(sketch, "E407.left", {"start": v(5.66, 0) * mm, "end": v(5.66, 6.36) * mm, "construction": true});
            skLineSegment(sketch, "E407.right", {"start": v(12.02, 0) * mm, "end": v(12.02, 6.36) * mm, "construction": true});
            skLineSegment(sketch, "E408", {"start": v(5.66, 0) * mm, "end": v(12.02, 6.36) * mm});
            skLineSegment(sketch, "E409", {"start": v(12.02, 6.36) * mm, "end": v(15.96, 10.3) * mm});
            skPoint(sketch, "E410", {"position": v(11.75, 18.81) * mm});
            skPoint(sketch, "E411", {"position": v(19.05, 11.99) * mm});
            skArc(sketch, "E412", {"start": v(15.96, 10.3) * mm, "mid": v(18.44, 11.4) * mm, "end": v(19.98, 13.6) * mm});
            skArc(sketch, "E413", {"start": v(13.62, 19.97) * mm, "mid": v(11.4, 18.43) * mm, "end": v(10.3, 15.95) * mm});
            skLineSegment(sketch, "E414", {"start": v(0, 5.66) * mm, "end": v(0, 0) * mm});
            skLineSegment(sketch, "E415", {"start": v(0, 0) * mm, "end": v(5.66, 0) * mm});
            skCircle(sketch, "E416", {"center": v(30.26, 30.25) * mm, "radius": 1.5 * mm});
            skCircle(sketch, "E417", {"center": v(15.26, 15.25) * mm, "radius": 1.5 * mm});
            skPoint(sketch, "E418", {"position": v(70.97, 90.96) * mm});
            skLineSegment(sketch, "E419", {"start": v(70.97, 86.46) * mm, "end": v(67.3, 86.02) * mm, "construction": true});
            skLineSegment(sketch, "E420", {"start": v(70.97, 86.46) * mm, "end": v(74.64, 86.02) * mm, "construction": true});
            skLineSegment(sketch, "E421", {"start": v(74.64, 86.02) * mm, "end": v(75.81, 84.1) * mm, "construction": true});
            skLineSegment(sketch, "E422", {"start": v(67.3, 86.02) * mm, "end": v(66.13, 84.1) * mm, "construction": true});
            skPoint(sketch, "E423", {"position": v(75.81, 84.1) * mm});
            skPoint(sketch, "E424", {"position": v(66.13, 84.1) * mm});
            skPoint(sketch, "E425", {"position": v(70.97, 89.22) * mm});
            skLineSegment(sketch, "E426", {"start": v(67.3, 86.02) * mm, "end": v(67.48, 84.52) * mm, "construction": true});
            skLineSegment(sketch, "E427", {"start": v(74.64, 86.02) * mm, "end": v(74.46, 84.52) * mm, "construction": true});
            skLineSegment(sketch, "E428", {"start": v(67.48, 84.52) * mm, "end": v(67.6, 83.52) * mm, "construction": true});
            skLineSegment(sketch, "E429", {"start": v(74.46, 84.52) * mm, "end": v(74.34, 83.52) * mm, "construction": true});
            skFitSpline(sketch, "E430", {"points": [v(67.48, 84.52) * mm, v(70.97, 89.22) * mm, v(74.46, 84.52) * mm], "startDerivative": vector(6.99, 14.1) * mm, "endDerivative": vector(6.99, -14.1) * mm});
            skLineSegment(sketch, "E431", {"start": v(67.6, 83.52) * mm, "end": v(74.34, 83.52) * mm, "construction": true});
            skPoint(sketch, "E432", {"position": v(70.97, 83.52) * mm});
            skFitSpline(sketch, "E433", {"points": [v(67.48, 84.52) * mm, v(70.97, 83.52) * mm, v(74.46, 84.52) * mm], "startDerivative": vector(0.72, -5.96) * mm, "endDerivative": vector(0.72, 5.96) * mm});
            skCircle(sketch, "E434", {"center": v(70.97, 78.96) * mm, "radius": 1.5 * mm, "construction": true});
            skCircle(sketch, "E435", {"center": v(70.97, 80.46) * mm, "radius": 1.5 * mm, "construction": true});
            skCircle(sketch, "E436", {"center": v(78.97, 70.96) * mm, "radius": 1.5 * mm, "construction": true});
            skCircle(sketch, "E437", {"center": v(80.47, 70.96) * mm, "radius": 1.5 * mm, "construction": true});
            skCircle(sketch, "E438", {"center": v(70.97, 62.96) * mm, "radius": 1.5 * mm, "construction": true});
            skCircle(sketch, "E439", {"center": v(70.97, 61.46) * mm, "radius": 1.5 * mm, "construction": true});
            skCircle(sketch, "E440", {"center": v(62.97, 70.96) * mm, "radius": 1.5 * mm, "construction": true});
            skCircle(sketch, "E441", {"center": v(61.47, 70.96) * mm, "radius": 1.5 * mm, "construction": true});
            skPoint(sketch, "E442", {"position": v(72.27, 79.71) * mm});
            skPoint(sketch, "E443", {"position": v(69.67, 79.71) * mm});
            skPoint(sketch, "E444", {"position": v(70.97, 81.96) * mm});
            skPoint(sketch, "E445", {"position": v(70.97, 77.46) * mm});
            skArc(sketch, "E446", {"start": v(69.67, 79.71) * mm, "mid": v(70.97, 77.46) * mm, "end": v(72.27, 79.71) * mm});
            skArc(sketch, "E447", {"start": v(72.27, 79.71) * mm, "mid": v(70.97, 81.96) * mm, "end": v(69.67, 79.71) * mm});
            skPoint(sketch, "E448", {"position": v(77.47, 70.96) * mm});
            skPoint(sketch, "E449", {"position": v(79.72, 72.26) * mm});
            skPoint(sketch, "E450", {"position": v(79.72, 69.66) * mm});
            skPoint(sketch, "E451", {"position": v(81.97, 70.96) * mm});
            skPoint(sketch, "E452", {"position": v(70.97, 59.96) * mm});
            skPoint(sketch, "E453", {"position": v(70.97, 64.46) * mm});
            skPoint(sketch, "E454", {"position": v(69.67, 62.21) * mm});
            skPoint(sketch, "E455", {"position": v(72.27, 62.21) * mm});
            skPoint(sketch, "E456", {"position": v(62.22, 72.26) * mm});
            skPoint(sketch, "E457", {"position": v(62.22, 69.66) * mm});
            skPoint(sketch, "E458", {"position": v(59.97, 70.96) * mm});
            skPoint(sketch, "E459", {"position": v(64.47, 70.96) * mm});
            skArc(sketch, "E460", {"start": v(62.22, 69.66) * mm, "mid": v(64.47, 70.96) * mm, "end": v(62.22, 72.26) * mm});
            skArc(sketch, "E461", {"start": v(62.22, 72.26) * mm, "mid": v(59.97, 70.96) * mm, "end": v(62.22, 69.66) * mm});
            skArc(sketch, "E462", {"start": v(79.72, 72.26) * mm, "mid": v(77.47, 70.96) * mm, "end": v(79.72, 69.66) * mm});
            skArc(sketch, "E463", {"start": v(79.72, 69.66) * mm, "mid": v(81.97, 70.96) * mm, "end": v(79.72, 72.26) * mm});
            skArc(sketch, "E464", {"start": v(69.67, 62.21) * mm, "mid": v(70.97, 59.96) * mm, "end": v(72.27, 62.21) * mm});
            skArc(sketch, "E465", {"start": v(72.27, 62.21) * mm, "mid": v(70.97, 64.46) * mm, "end": v(69.67, 62.21) * mm});
            skLineSegment(sketch, "E466", {"start": v(76.22, 90.26) * mm, "end": v(80.87, 80.86) * mm});
            skPoint(sketch, "E467", {"position": v(82.74, 78.54) * mm});
            skArc(sketch, "E468", {"start": v(84.09, 75.85) * mm, "mid": v(82.75, 78.53) * mm, "end": v(80.87, 80.86) * mm});
            skPoint(sketch, "E469", {"position": v(84.95, 71.78) * mm});
            skPoint(sketch, "E470", {"position": v(86.47, 70.96) * mm});
            skPoint(sketch, "E471", {"position": v(82.4, 64.55) * mm});
            skFitSpline(sketch, "E472", {"points": [v(84.95, 71.78) * mm, v(86.47, 70.96) * mm, v(82.4, 64.55) * mm], "startDerivative": vector(7.9, -0.91) * mm, "endDerivative": vector(-10.03, -8.08) * mm});
            skPoint(sketch, "E473", {"position": v(83.76, 70.96) * mm});
            skFitSpline(sketch, "E474", {"points": [v(82.4, 64.55) * mm, v(83.76, 70.96) * mm, v(84.95, 71.78) * mm], "startDerivative": vector(-7.12, -6.6) * mm, "endDerivative": vector(6.93, -0.38) * mm});
            skFitSpline(sketch, "E475", {"points": [v(63.66, 53.75) * mm, v(68.49, 55.66) * mm], "startDerivative": vector(5.12, 3.73) * mm, "endDerivative": vector(5.29, 1) * mm});
            skSolve(sketch);
        }
        {
            var Q0;
            Q0=qSketchRegion(id+"F0",true);
            extrude(context, id + "F2", {"entities" : qUnion([Q0]), "depth" : 2 * mm});
        }
        {
            var Q0;
            Q0=qCreatedBy(makeId("Top.planeOp"),FACE);
            var sketch = newSketch(context, id + "F3", { "sketchPlane" : qUnion([Q0])});
            skLineSegment(sketch, "E476.bottom", {"start": v(-15.25, 15.25) * mm, "end": v(15.25, 15.25) * mm, "construction": true});
            skLineSegment(sketch, "E476.top", {"start": v(-15.25, -15.25) * mm, "end": v(15.25, -15.25) * mm, "construction": true});
            skLineSegment(sketch, "E476.left", {"start": v(-15.25, 15.25) * mm, "end": v(-15.25, -15.25) * mm, "construction": true});
            skLineSegment(sketch, "E476.right", {"start": v(15.25, 15.25) * mm, "end": v(15.25, -15.25) * mm, "construction": true});
            skPoint(sketch, "E476.middle", {"position": v(0, 0) * mm});
            skLineSegment(sketch, "E477.bottom", {"start": v(30.25, 30.25) * mm, "end": v(-30.25, 30.25) * mm, "construction": true});
            skLineSegment(sketch, "E477.top", {"start": v(30.25, -30.25) * mm, "end": v(-30.25, -30.25) * mm, "construction": true});
            skLineSegment(sketch, "E477.left", {"start": v(30.25, 30.25) * mm, "end": v(30.25, -30.25) * mm, "construction": true});
            skLineSegment(sketch, "E477.right", {"start": v(-30.25, 30.25) * mm, "end": v(-30.25, -30.25) * mm, "construction": true});
            skLineSegment(sketch, "E478.bottom", {"start": v(-70.96, 70.96) * mm, "end": v(70.96, 70.96) * mm, "construction": true});
            skLineSegment(sketch, "E478.top", {"start": v(-70.96, -70.96) * mm, "end": v(70.96, -70.96) * mm, "construction": true});
            skLineSegment(sketch, "E478.left", {"start": v(-70.96, 70.96) * mm, "end": v(-70.96, -70.96) * mm, "construction": true});
            skLineSegment(sketch, "E478.right", {"start": v(70.96, 70.96) * mm, "end": v(70.96, -70.96) * mm, "construction": true});
            skCircle(sketch, "E479", {"center": v(70.96, 70.96) * mm, "radius": 4.5 * mm, "construction": true});
            skCircle(sketch, "E480", {"center": v(-70.96, 70.96) * mm, "radius": 4.5 * mm, "construction": true});
            skCircle(sketch, "E481", {"center": v(70.96, -70.96) * mm, "radius": 4.5 * mm, "construction": true});
            skCircle(sketch, "E482", {"center": v(-70.96, -70.96) * mm, "radius": 4.5 * mm, "construction": true});
            skCircle(sketch, "E483", {"center": v(70.96, 70.96) * mm, "radius": 8 * mm, "construction": true});
            skCircle(sketch, "E484", {"center": v(70.96, -70.96) * mm, "radius": 8 * mm, "construction": true});
            skCircle(sketch, "E485", {"center": v(-70.96, -70.96) * mm, "radius": 8 * mm, "construction": true});
            skCircle(sketch, "E486", {"center": v(-70.96, 70.96) * mm, "radius": 8 * mm, "construction": true});
            skCircle(sketch, "E487", {"center": v(70.96, 70.96) * mm, "radius": 9.5 * mm, "construction": true});
            skCircle(sketch, "E488", {"center": v(70.96, -70.96) * mm, "radius": 9.5 * mm, "construction": true});
            skCircle(sketch, "E489", {"center": v(-70.96, -70.96) * mm, "radius": 9.5 * mm, "construction": true});
            skCircle(sketch, "E490", {"center": v(-70.96, 70.96) * mm, "radius": 9.5 * mm, "construction": true});
            skCircle(sketch, "E491", {"center": v(70.96, 70.96) * mm, "radius": 14 * mm, "construction": true});
            skCircle(sketch, "E492", {"center": v(-70.96, 70.96) * mm, "radius": 14 * mm, "construction": true});
            skCircle(sketch, "E493", {"center": v(70.96, -70.96) * mm, "radius": 14 * mm, "construction": true});
            skCircle(sketch, "E494", {"center": v(-70.96, -70.96) * mm, "radius": 14 * mm, "construction": true});
            skCircle(sketch, "E495", {"center": v(70.96, 70.96) * mm, "radius": 63.5 * mm, "construction": true});
            skCircle(sketch, "E496", {"center": v(70.96, -70.96) * mm, "radius": 63.5 * mm, "construction": true});
            skCircle(sketch, "E497", {"center": v(-70.96, -70.96) * mm, "radius": 63.5 * mm, "construction": true});
            skCircle(sketch, "E498", {"center": v(-70.96, 70.96) * mm, "radius": 63.5 * mm, "construction": true});
            skLineSegment(sketch, "E499", {"start": v(0, 30.25) * mm, "end": v(0, 36.4) * mm, "construction": true});
            skLineSegment(sketch, "E500", {"start": v(0, 36.4) * mm, "end": v(-14.3, 36.4) * mm, "construction": true});
            skLineSegment(sketch, "E501", {"start": v(0, 36.4) * mm, "end": v(14.29, 36.4) * mm, "construction": true});
            skLineSegment(sketch, "E502", {"start": v(0, -30.25) * mm, "end": v(0, -36.4) * mm, "construction": true});
            skLineSegment(sketch, "E503", {"start": v(0, -36.4) * mm, "end": v(-14.29, -36.4) * mm, "construction": true});
            skLineSegment(sketch, "E504", {"start": v(0, -36.4) * mm, "end": v(14.3, -36.4) * mm, "construction": true});
            skLineSegment(sketch, "E505.bottom", {"start": v(-26.2, 26.2) * mm, "end": v(26.2, 26.2) * mm, "construction": true});
            skLineSegment(sketch, "E505.top", {"start": v(-26.2, -26.19) * mm, "end": v(26.2, -26.19) * mm, "construction": true});
            skLineSegment(sketch, "E505.left", {"start": v(-26.2, 26.2) * mm, "end": v(-26.2, -26.19) * mm, "construction": true});
            skLineSegment(sketch, "E505.right", {"start": v(26.2, 26.2) * mm, "end": v(26.2, -26.2) * mm, "construction": true});
            skCircle(sketch, "E506", {"center": v(30.25, 30.25) * mm, "radius": 5 * mm, "construction": true});
            skCircle(sketch, "E507", {"center": v(-30.25, 30.25) * mm, "radius": 5 * mm, "construction": true});
            skCircle(sketch, "E508", {"center": v(30.25, -30.25) * mm, "radius": 5 * mm, "construction": true});
            skCircle(sketch, "E509", {"center": v(-30.25, -30.25) * mm, "radius": 5 * mm, "construction": true});
            skLineSegment(sketch, "E510", {"start": v(-26.19, 26.2) * mm, "end": v(-30.25, 30.25) * mm, "construction": true});
            skLineSegment(sketch, "E511", {"start": v(-26.71, 26.71) * mm, "end": v(-33.79, 33.79) * mm, "construction": true});
            skLineSegment(sketch, "E512", {"start": v(-31.46, 31.46) * mm, "end": v(-28.13, 34.78) * mm, "construction": true});
            skLineSegment(sketch, "E513", {"start": v(-31.46, 31.46) * mm, "end": v(-34.78, 28.13) * mm, "construction": true});
            skLineSegment(sketch, "E514", {"start": v(26.2, 26.2) * mm, "end": v(30.25, 30.25) * mm, "construction": true});
            skLineSegment(sketch, "E515", {"start": v(26.71, 26.71) * mm, "end": v(33.79, 33.79) * mm, "construction": true});
            skLineSegment(sketch, "E516", {"start": v(31.46, 31.46) * mm, "end": v(34.78, 28.13) * mm, "construction": true});
            skLineSegment(sketch, "E517", {"start": v(31.46, 31.46) * mm, "end": v(28.13, 34.78) * mm, "construction": true});
            skLineSegment(sketch, "E518", {"start": v(26.19, -26.19) * mm, "end": v(30.25, -30.25) * mm, "construction": true});
            skLineSegment(sketch, "E519", {"start": v(26.71, -26.71) * mm, "end": v(33.79, -33.79) * mm, "construction": true});
            skLineSegment(sketch, "E520", {"start": v(31.46, -31.46) * mm, "end": v(34.78, -28.13) * mm, "construction": true});
            skLineSegment(sketch, "E521", {"start": v(31.46, -31.46) * mm, "end": v(28.13, -34.78) * mm, "construction": true});
            skLineSegment(sketch, "E522", {"start": v(-26.2, -26.2) * mm, "end": v(-30.25, -30.25) * mm, "construction": true});
            skLineSegment(sketch, "E523", {"start": v(-26.71, -26.71) * mm, "end": v(-33.79, -33.79) * mm, "construction": true});
            skLineSegment(sketch, "E524", {"start": v(-31.46, -31.46) * mm, "end": v(-28.13, -34.78) * mm, "construction": true});
            skLineSegment(sketch, "E525", {"start": v(-31.46, -31.46) * mm, "end": v(-34.78, -28.13) * mm, "construction": true});
            skArc(sketch, "E526", {"start": v(-28.13, 34.78) * mm, "mid": v(-33.79, 33.79) * mm, "end": v(-34.78, 28.13) * mm});
            skArc(sketch, "E527", {"start": v(34.78, 28.13) * mm, "mid": v(33.79, 33.79) * mm, "end": v(28.13, 34.78) * mm});
            skArc(sketch, "E528", {"start": v(28.13, -34.78) * mm, "mid": v(33.79, -33.79) * mm, "end": v(34.78, -28.13) * mm});
            skArc(sketch, "E529", {"start": v(-34.78, -28.13) * mm, "mid": v(-33.79, -33.79) * mm, "end": v(-28.13, -34.78) * mm});
            skLineSegment(sketch, "E530.bottom", {"start": v(24.5, -24.5) * mm, "end": v(-24.5, -24.5) * mm, "construction": true});
            skLineSegment(sketch, "E530.top", {"start": v(24.5, 24.5) * mm, "end": v(-24.5, 24.5) * mm, "construction": true});
            skLineSegment(sketch, "E530.left", {"start": v(24.5, -24.5) * mm, "end": v(24.5, 24.5) * mm, "construction": true});
            skLineSegment(sketch, "E530.right", {"start": v(-24.5, -24.5) * mm, "end": v(-24.5, 24.5) * mm, "construction": true});
            skLineSegment(sketch, "E531", {"start": v(34.78, 28.13) * mm, "end": v(28.26, 10.3) * mm});
            skLineSegment(sketch, "E532", {"start": v(28.26, -10.3) * mm, "end": v(34.78, -28.13) * mm});
            skLineSegment(sketch, "E533", {"start": v(-34.78, -28.13) * mm, "end": v(-28.26, -10.3) * mm});
            skLineSegment(sketch, "E534", {"start": v(-28.26, 10.3) * mm, "end": v(-34.78, 28.13) * mm});
            skPoint(sketch, "E535.visualSharp", {"position": v(24.5, 0) * mm});
            skArc(sketch, "E535.filletArc", {"start": v(28.26, 10.3) * mm, "mid": v(26.44, 0) * mm, "end": v(28.26, -10.3) * mm});
            skPoint(sketch, "E536.visualSharp", {"position": v(-24.5, 0) * mm});
            skArc(sketch, "E536.filletArc", {"start": v(-28.26, -10.3) * mm, "mid": v(-26.44, 0) * mm, "end": v(-28.26, 10.3) * mm});
            skPoint(sketch, "E537.visualSharp", {"position": v(0, -24.5) * mm});
            skLineSegment(sketch, "E538", {"start": v(-28.13, 34.78) * mm, "end": v(-11.4, 23.17) * mm});
            skLineSegment(sketch, "E539", {"start": v(11.4, 23.17) * mm, "end": v(28.13, 34.78) * mm});
            skPoint(sketch, "E540.visualSharp", {"position": v(0, 15.25) * mm});
            skArc(sketch, "E540.filletArc", {"start": v(-11.4, 23.17) * mm, "mid": v(0, 19.6) * mm, "end": v(11.4, 23.17) * mm});
            skCircle(sketch, "E541", {"center": v(-30.25, 30.25) * mm, "radius": 1.5 * mm});
            skCircle(sketch, "E542", {"center": v(-15.25, 15.25) * mm, "radius": 1.5 * mm});
            skCircle(sketch, "E543", {"center": v(15.25, 15.25) * mm, "radius": 1.5 * mm});
            skCircle(sketch, "E544", {"center": v(30.25, 30.25) * mm, "radius": 1.5 * mm});
            skCircle(sketch, "E545", {"center": v(30.25, -30.25) * mm, "radius": 1.5 * mm});
            skCircle(sketch, "E546", {"center": v(15.25, -15.25) * mm, "radius": 1.5 * mm});
            skCircle(sketch, "E547", {"center": v(-15.25, -15.25) * mm, "radius": 1.5 * mm});
            skCircle(sketch, "E548", {"center": v(-30.25, -30.25) * mm, "radius": 1.5 * mm});
            skLineSegment(sketch, "E549", {"start": v(-28.13, -34.78) * mm, "end": v(-11.4, -23.17) * mm});
            skLineSegment(sketch, "E550", {"start": v(11.4, -23.17) * mm, "end": v(28.13, -34.78) * mm});
            skPoint(sketch, "E551.visualSharp", {"position": v(0, -15.25) * mm});
            skArc(sketch, "E551.filletArc", {"start": v(11.4, -23.17) * mm, "mid": v(0, -19.6) * mm, "end": v(-11.4, -23.17) * mm});
            skSolve(sketch);
        }
        {
            var Q0;
            Q0=qSketchRegion(id+"F1",true);
            extrude(context, id + "F4", {"entities" : qUnion([Q0]), "operationType" : NewBodyOperationType.ADD, "depth" : 7 * mm, "hasSecondDirection" : true, "secondDirectionOppositeDirection" : false, "secondDirectionDepth" : 3 * mm});
        }
        {
            var Q0;
            Q0=qCreatedBy(makeId("Top.planeOp"),FACE);
            var sketch = newSketch(context, id + "F5", { "sketchPlane" : qUnion([Q0])});
            skLineSegment(sketch, "E552.bottom", {"start": v(-15.28, 17.52) * mm, "end": v(15.22, 17.52) * mm, "construction": true});
            skLineSegment(sketch, "E552.top", {"start": v(-15.25, -12.98) * mm, "end": v(15.25, -12.98) * mm, "construction": true});
            skLineSegment(sketch, "E552.left", {"start": v(-15.25, 17.52) * mm, "end": v(-15.25, -12.98) * mm, "construction": true});
            skLineSegment(sketch, "E552.right", {"start": v(15.22, 17.52) * mm, "end": v(15.22, -12.98) * mm, "construction": true});
            skPoint(sketch, "E552.middle", {"position": v(-0.01, 2.27) * mm});
            skLineSegment(sketch, "E553.bottom", {"start": v(30.24, 32.52) * mm, "end": v(-30.26, 32.52) * mm, "construction": true});
            skLineSegment(sketch, "E553.top", {"start": v(30.24, -27.98) * mm, "end": v(-30.26, -27.98) * mm, "construction": true});
            skLineSegment(sketch, "E553.left", {"start": v(30.24, 32.52) * mm, "end": v(30.24, -27.98) * mm, "construction": true});
            skLineSegment(sketch, "E553.right", {"start": v(-30.26, 32.52) * mm, "end": v(-30.26, -27.98) * mm, "construction": true});
            skLineSegment(sketch, "E554.bottom", {"start": v(-70.97, 73.23) * mm, "end": v(70.95, 73.23) * mm, "construction": true});
            skLineSegment(sketch, "E554.top", {"start": v(-70.97, -68.69) * mm, "end": v(70.95, -68.69) * mm, "construction": true});
            skLineSegment(sketch, "E554.left", {"start": v(-70.97, 73.23) * mm, "end": v(-70.97, -68.69) * mm, "construction": true});
            skLineSegment(sketch, "E554.right", {"start": v(70.95, 73.23) * mm, "end": v(70.95, -68.69) * mm, "construction": true});
            skCircle(sketch, "E555", {"center": v(70.95, 73.23) * mm, "radius": 8 * mm, "construction": true});
            skCircle(sketch, "E556", {"center": v(70.95, -68.69) * mm, "radius": 8 * mm, "construction": true});
            skCircle(sketch, "E557", {"center": v(-70.97, -68.69) * mm, "radius": 8 * mm, "construction": true});
            skCircle(sketch, "E558", {"center": v(-70.97, 73.23) * mm, "radius": 8 * mm, "construction": true});
            skCircle(sketch, "E559", {"center": v(70.95, 73.23) * mm, "radius": 9.5 * mm, "construction": true});
            skCircle(sketch, "E560", {"center": v(70.95, -68.69) * mm, "radius": 9.5 * mm, "construction": true});
            skCircle(sketch, "E561", {"center": v(-70.97, -68.69) * mm, "radius": 9.5 * mm, "construction": true});
            skCircle(sketch, "E562", {"center": v(-70.97, 73.23) * mm, "radius": 9.5 * mm, "construction": true});
            skCircle(sketch, "E563", {"center": v(70.95, 73.23) * mm, "radius": 14 * mm, "construction": true});
            skCircle(sketch, "E564", {"center": v(-70.97, 73.23) * mm, "radius": 14 * mm, "construction": true});
            skCircle(sketch, "E565", {"center": v(70.95, -68.69) * mm, "radius": 14 * mm, "construction": true});
            skCircle(sketch, "E566", {"center": v(-70.97, -68.69) * mm, "radius": 14 * mm, "construction": true});
            skCircle(sketch, "E567", {"center": v(70.95, 73.23) * mm, "radius": 63.5 * mm, "construction": true});
            skCircle(sketch, "E568", {"center": v(70.95, -68.69) * mm, "radius": 63.5 * mm, "construction": true});
            skCircle(sketch, "E569", {"center": v(-70.97, -68.69) * mm, "radius": 63.5 * mm, "construction": true});
            skCircle(sketch, "E570", {"center": v(-70.97, 73.23) * mm, "radius": 63.5 * mm, "construction": true});
            skLineSegment(sketch, "E571", {"start": v(-0.01, 32.52) * mm, "end": v(-0.01, 40.03) * mm, "construction": true});
            skLineSegment(sketch, "E572", {"start": v(-0.01, -27.98) * mm, "end": v(-0.01, -35.48) * mm, "construction": true});
            skLineSegment(sketch, "E573.bottom", {"start": v(-26.18, 28.53) * mm, "end": v(26.2, 28.53) * mm, "construction": true});
            skLineSegment(sketch, "E573.top", {"start": v(-26.22, -23.98) * mm, "end": v(26.16, -23.98) * mm, "construction": true});
            skLineSegment(sketch, "E573.left", {"start": v(-26.18, 28.53) * mm, "end": v(-26.18, -23.85) * mm, "construction": true});
            skLineSegment(sketch, "E573.right", {"start": v(26.2, 28.53) * mm, "end": v(26.2, -23.92) * mm, "construction": true});
            skCircle(sketch, "E574", {"center": v(30.24, 32.52) * mm, "radius": 5 * mm, "construction": true});
            skCircle(sketch, "E575", {"center": v(-30.26, 32.52) * mm, "radius": 5 * mm, "construction": true});
            skCircle(sketch, "E576", {"center": v(30.24, -27.98) * mm, "radius": 5 * mm, "construction": true});
            skCircle(sketch, "E577", {"center": v(-30.26, -27.98) * mm, "radius": 5 * mm, "construction": true});
            skLineSegment(sketch, "E578.bottom", {"start": v(24.49, 26.77) * mm, "end": v(-24.51, 26.77) * mm, "construction": true});
            skLineSegment(sketch, "E578.top", {"start": v(24.49, -22.23) * mm, "end": v(-24.51, -22.23) * mm, "construction": true});
            skLineSegment(sketch, "E578.left", {"start": v(24.49, 26.77) * mm, "end": v(24.49, -22.23) * mm, "construction": true});
            skLineSegment(sketch, "E578.right", {"start": v(-24.51, 26.77) * mm, "end": v(-24.51, -22.23) * mm, "construction": true});
            skLineSegment(sketch, "E579", {"start": v(-26.18, 28.53) * mm, "end": v(-30.26, 32.52) * mm, "construction": true});
            skLineSegment(sketch, "E580", {"start": v(-26.7, 29.02) * mm, "end": v(-33.83, 36.02) * mm, "construction": true});
            skLineSegment(sketch, "E581", {"start": v(-31.82, 34.05) * mm, "end": v(-28.67, 37.26) * mm, "construction": true});
            skLineSegment(sketch, "E582", {"start": v(-31.82, 34.05) * mm, "end": v(-34.97, 30.83) * mm, "construction": true});
            skArc(sketch, "E583", {"start": v(-28.67, 37.26) * mm, "mid": v(-33.83, 36.02) * mm, "end": v(-34.97, 30.83) * mm});
            skLineSegment(sketch, "E584", {"start": v(26.2, 28.53) * mm, "end": v(30.24, 32.52) * mm, "construction": true});
            skLineSegment(sketch, "E585", {"start": v(26.68, 29) * mm, "end": v(33.8, 36.04) * mm, "construction": true});
            skLineSegment(sketch, "E586", {"start": v(31.79, 34.06) * mm, "end": v(34.95, 30.86) * mm, "construction": true});
            skLineSegment(sketch, "E587", {"start": v(31.79, 34.06) * mm, "end": v(28.62, 37.26) * mm, "construction": true});
            skArc(sketch, "E588", {"start": v(34.95, 30.86) * mm, "mid": v(33.8, 36.04) * mm, "end": v(28.62, 37.26) * mm});
            skLineSegment(sketch, "E589", {"start": v(26.16, -23.98) * mm, "end": v(30.24, -27.98) * mm, "construction": true});
            skLineSegment(sketch, "E590", {"start": v(26.67, -24.48) * mm, "end": v(33.8, -31.48) * mm, "construction": true});
            skLineSegment(sketch, "E591", {"start": v(31.8, -29.5) * mm, "end": v(34.94, -26.29) * mm, "construction": true});
            skLineSegment(sketch, "E592", {"start": v(31.8, -29.5) * mm, "end": v(28.64, -32.72) * mm, "construction": true});
            skArc(sketch, "E593", {"start": v(28.64, -32.72) * mm, "mid": v(33.8, -31.48) * mm, "end": v(34.94, -26.29) * mm});
            skLineSegment(sketch, "E594", {"start": v(-26.22, -23.98) * mm, "end": v(-30.26, -27.98) * mm, "construction": true});
            skLineSegment(sketch, "E595", {"start": v(-26.7, -24.46) * mm, "end": v(-33.82, -31.5) * mm, "construction": true});
            skLineSegment(sketch, "E596", {"start": v(-31.81, -29.5) * mm, "end": v(-28.65, -32.7) * mm, "construction": true});
            skLineSegment(sketch, "E597", {"start": v(-31.81, -29.5) * mm, "end": v(-34.98, -26.31) * mm, "construction": true});
            skArc(sketch, "E598", {"start": v(-34.98, -26.31) * mm, "mid": v(-33.82, -31.5) * mm, "end": v(-28.65, -32.7) * mm});
            skLineSegment(sketch, "E599", {"start": v(-34.98, -26.31) * mm, "end": v(-28.29, -8.04) * mm});
            skLineSegment(sketch, "E600", {"start": v(-28.29, 12.59) * mm, "end": v(-34.97, 30.83) * mm});
            skLineSegment(sketch, "E601", {"start": v(34.95, 30.86) * mm, "end": v(28.26, 12.59) * mm});
            skLineSegment(sketch, "E602", {"start": v(28.26, -8.04) * mm, "end": v(34.94, -26.29) * mm});
            skPoint(sketch, "E603.visualSharp", {"position": v(24.49, 2.27) * mm});
            skArc(sketch, "E603.filletArc", {"start": v(28.26, 12.59) * mm, "mid": v(26.43, 2.27) * mm, "end": v(28.26, -8.04) * mm});
            skPoint(sketch, "E604.visualSharp", {"position": v(-24.51, 2.27) * mm});
            skArc(sketch, "E604.filletArc", {"start": v(-28.29, -8.04) * mm, "mid": v(-26.46, 2.27) * mm, "end": v(-28.29, 12.59) * mm});
            skLineSegment(sketch, "E605", {"start": v(-15.28, 22) * mm, "end": v(15.22, 22) * mm, "construction": true});
            skPoint(sketch, "E606.endSnap0", {"position": v(0, -12.98) * mm});
            skLineSegment(sketch, "E607", {"start": v(-15.25, -17.43) * mm, "end": v(15.25, -17.43) * mm, "construction": true});
            skLineSegment(sketch, "E608", {"start": v(-14.34, -35.48) * mm, "end": v(14.32, -35.48) * mm, "construction": true});
            skCircle(sketch, "E609", {"center": v(-30.26, 32.52) * mm, "radius": 1.5 * mm});
            skCircle(sketch, "E610", {"center": v(30.24, 32.52) * mm, "radius": 1.5 * mm});
            skCircle(sketch, "E611", {"center": v(15.22, 17.52) * mm, "radius": 1.5 * mm});
            skCircle(sketch, "E612", {"center": v(-15.28, 17.52) * mm, "radius": 1.5 * mm});
            skCircle(sketch, "E613", {"center": v(-15.25, -12.98) * mm, "radius": 1.5 * mm});
            skCircle(sketch, "E614", {"center": v(15.25, -12.98) * mm, "radius": 1.5 * mm});
            skCircle(sketch, "E615", {"center": v(30.24, -27.98) * mm, "radius": 1.5 * mm});
            skCircle(sketch, "E616", {"center": v(-30.26, -27.98) * mm, "radius": 1.5 * mm});
            skLineSegment(sketch, "E617", {"start": v(14.32, 40.03) * mm, "end": v(10.32, 40.03) * mm, "construction": true});
            skLineSegment(sketch, "E618", {"start": v(-14.34, 40.03) * mm, "end": v(-10.34, 40.03) * mm, "construction": true});
            skLineSegment(sketch, "E619", {"start": v(10.32, 40.03) * mm, "end": v(10.32, 36.03) * mm, "construction": true});
            skLineSegment(sketch, "E620", {"start": v(-10.34, 40.03) * mm, "end": v(-10.34, 36.03) * mm, "construction": true});
            skLineSegment(sketch, "E621", {"start": v(-0.01, 40.03) * mm, "end": v(-0.03, 17.52) * mm, "construction": true});
            skPoint(sketch, "E622.visualSharp", {"position": v(-14.34, -35.48) * mm});
            skPoint(sketch, "E623.visualSharp", {"position": v(14.32, -35.48) * mm});
            skCircle(sketch, "E624", {"center": v(-0.01, 2.27) * mm, "radius": 17.1 * mm, "construction": true});
            skLineSegment(sketch, "E625", {"start": v(-0.01, 2.27) * mm, "end": v(14.08, 16.37) * mm, "construction": true});
            skLineSegment(sketch, "E626", {"start": v(-0.01, 2.27) * mm, "end": v(-15.28, 17.52) * mm, "construction": true});
            skLineSegment(sketch, "E627", {"start": v(-0.01, 2.27) * mm, "end": v(-15.32, -13.05) * mm, "construction": true});
            skLineSegment(sketch, "E628", {"start": v(-0.01, 2.27) * mm, "end": v(15.25, -12.98) * mm, "construction": true});
            skLineSegment(sketch, "E629", {"start": v(-10.71, 12.96) * mm, "end": v(-7.89, 15.8) * mm, "construction": true});
            skLineSegment(sketch, "E630", {"start": v(-10.71, 12.96) * mm, "end": v(-13.54, 10.13) * mm, "construction": true});
            skLineSegment(sketch, "E631", {"start": v(9.01, 11.3) * mm, "end": v(11.84, 8.47) * mm, "construction": true});
            skLineSegment(sketch, "E632", {"start": v(9.01, 11.3) * mm, "end": v(6.19, 14.13) * mm, "construction": true});
            skLineSegment(sketch, "E633", {"start": v(9.8, -7.53) * mm, "end": v(12.63, -4.7) * mm, "construction": true});
            skLineSegment(sketch, "E634", {"start": v(9.8, -7.53) * mm, "end": v(6.97, -10.36) * mm, "construction": true});
            skLineSegment(sketch, "E635", {"start": v(-9.52, -7.25) * mm, "end": v(-6.7, -10.07) * mm, "construction": true});
            skLineSegment(sketch, "E636", {"start": v(-9.52, -7.25) * mm, "end": v(-12.35, -4.42) * mm, "construction": true});
            skLineSegment(sketch, "E637.bottom", {"start": v(6.34, 8.62) * mm, "end": v(-6.36, 8.62) * mm, "construction": true});
            skLineSegment(sketch, "E637.top", {"start": v(6.34, -4.08) * mm, "end": v(-6.36, -4.08) * mm, "construction": true});
            skLineSegment(sketch, "E637.left", {"start": v(6.34, 8.62) * mm, "end": v(6.34, -4.08) * mm, "construction": true});
            skLineSegment(sketch, "E637.right", {"start": v(-6.36, 8.62) * mm, "end": v(-6.36, -4.08) * mm, "construction": true});
            skLineSegment(sketch, "E638", {"start": v(6.19, 14.13) * mm, "end": v(8.92, 16.86) * mm, "construction": true});
            skLineSegment(sketch, "E639", {"start": v(11.84, 8.47) * mm, "end": v(14.57, 11.2) * mm, "construction": true});
            skLineSegment(sketch, "E640", {"start": v(7.98, 15.92) * mm, "end": v(1.4, 9.34) * mm});
            skLineSegment(sketch, "E641", {"start": v(-1.43, 9.34) * mm, "end": v(-8, 15.92) * mm});
            skLineSegment(sketch, "E642", {"start": v(-13.54, 10.13) * mm, "end": v(-14.6, 11.2) * mm, "construction": true});
            skLineSegment(sketch, "E643", {"start": v(-6.7, -10.07) * mm, "end": v(-8.93, -12.32) * mm, "construction": true});
            skLineSegment(sketch, "E644", {"start": v(-8, -11.38) * mm, "end": v(-1.43, -4.8) * mm});
            skLineSegment(sketch, "E645", {"start": v(1.4, -4.8) * mm, "end": v(7.98, -11.37) * mm});
            skLineSegment(sketch, "E646", {"start": v(13.64, 10.27) * mm, "end": v(7.06, 3.69) * mm});
            skLineSegment(sketch, "E647", {"start": v(7.06, 0.86) * mm, "end": v(13.64, -5.72) * mm});
            skPoint(sketch, "E648", {"position": v(-7.75, 17.52) * mm});
            skPoint(sketch, "E649", {"position": v(7.72, 17.52) * mm});
            skPoint(sketch, "E650", {"position": v(15.22, 10.04) * mm});
            skPoint(sketch, "E651", {"position": v(15.22, -5.5) * mm});
            skPoint(sketch, "E652", {"position": v(7.72, -12.98) * mm});
            skPoint(sketch, "E653", {"position": v(-7.75, -12.98) * mm});
            skPoint(sketch, "E654", {"position": v(-15.25, -5.5) * mm});
            skPoint(sketch, "E655", {"position": v(-15.25, 10.04) * mm});
            skLineSegment(sketch, "E656", {"start": v(-7.79, 17.5) * mm, "end": v(-7.75, 17.52) * mm});
            skLineSegment(sketch, "E657", {"start": v(7.76, 17.5) * mm, "end": v(7.72, 17.52) * mm});
            skLineSegment(sketch, "E658", {"start": v(15.22, 10.05) * mm, "end": v(15.22, 10.04) * mm});
            skLineSegment(sketch, "E659", {"start": v(15.22, -5.5) * mm, "end": v(15.22, -5.5) * mm});
            skLineSegment(sketch, "E660", {"start": v(7.76, -12.96) * mm, "end": v(7.72, -12.98) * mm});
            skLineSegment(sketch, "E661", {"start": v(-7.75, -12.98) * mm, "end": v(-7.78, -12.96) * mm});
            skLineSegment(sketch, "E662", {"start": v(-15.24, -5.5) * mm, "end": v(-15.25, -5.5) * mm});
            skLineSegment(sketch, "E663", {"start": v(-15.24, 10.05) * mm, "end": v(-15.25, 10.04) * mm});
            skPoint(sketch, "E664", {"position": v(-0.03, 19.37) * mm});
            skPoint(sketch, "E665", {"position": v(17.09, 2.27) * mm});
            skPoint(sketch, "E666", {"position": v(-17.11, 2.27) * mm});
            skPoint(sketch, "E667", {"position": v(-0.01, -14.83) * mm});
            skArc(sketch, "E668", {"start": v(15.22, -5.5) * mm, "mid": v(17.09, 2.27) * mm, "end": v(15.22, 10.04) * mm});
            skArc(sketch, "E669", {"start": v(-15.25, 10.04) * mm, "mid": v(-17.11, 2.27) * mm, "end": v(-15.25, -5.5) * mm});
            skPoint(sketch, "E670.visualSharp", {"position": v(-5.66, 2.27) * mm});
            skPoint(sketch, "E671.visualSharp", {"position": v(-14.6, 11.2) * mm});
            skArc(sketch, "E671.filletArc", {"start": v(-13.66, 10.27) * mm, "mid": v(-14.5, 10.55) * mm, "end": v(-15.24, 10.05) * mm});
            skPoint(sketch, "E672.visualSharp", {"position": v(-14.6, -6.66) * mm});
            skArc(sketch, "E672.filletArc", {"start": v(-15.24, -5.5) * mm, "mid": v(-14.5, -6.01) * mm, "end": v(-13.66, -5.73) * mm});
            skPoint(sketch, "E673.visualSharp", {"position": v(-8.94, 16.86) * mm});
            skArc(sketch, "E673.filletArc", {"start": v(-7.79, 17.5) * mm, "mid": v(-8.3, 16.77) * mm, "end": v(-8, 15.92) * mm});
            skPoint(sketch, "E674.visualSharp", {"position": v(8.92, 16.86) * mm});
            skArc(sketch, "E674.filletArc", {"start": v(7.98, 15.92) * mm, "mid": v(8.26, 16.77) * mm, "end": v(7.76, 17.5) * mm});
            skPoint(sketch, "E675.visualSharp", {"position": v(14.57, -6.66) * mm});
            skArc(sketch, "E675.filletArc", {"start": v(13.64, -5.72) * mm, "mid": v(14.48, -6) * mm, "end": v(15.22, -5.5) * mm});
            skPoint(sketch, "E676.visualSharp", {"position": v(14.57, 11.2) * mm});
            skArc(sketch, "E676.filletArc", {"start": v(15.22, 10.05) * mm, "mid": v(14.48, 10.55) * mm, "end": v(13.64, 10.27) * mm});
            skPoint(sketch, "E677.visualSharp", {"position": v(8.92, -12.3) * mm});
            skArc(sketch, "E677.filletArc", {"start": v(7.76, -12.96) * mm, "mid": v(8.27, -12.22) * mm, "end": v(7.98, -11.37) * mm});
            skPoint(sketch, "E678.visualSharp", {"position": v(-8.93, -12.32) * mm});
            skArc(sketch, "E678.filletArc", {"start": v(-8, -11.38) * mm, "mid": v(-8.28, -12.23) * mm, "end": v(-7.78, -12.96) * mm});
            skLineSegment(sketch, "E679", {"start": v(-13.66, 10.27) * mm, "end": v(-7.08, 3.68) * mm});
            skLineSegment(sketch, "E680", {"start": v(-13.66, -5.73) * mm, "end": v(-7.08, 0.86) * mm});
            skArc(sketch, "E681.filletArc", {"start": v(-7.08, 0.86) * mm, "mid": v(-6.5, 2.27) * mm, "end": v(-7.08, 3.68) * mm});
            skPoint(sketch, "E682.visualSharp", {"position": v(-0.01, -3.39) * mm});
            skArc(sketch, "E682.filletArc", {"start": v(1.4, -4.8) * mm, "mid": v(-0.01, -4.22) * mm, "end": v(-1.43, -4.8) * mm});
            skPoint(sketch, "E683.visualSharp", {"position": v(5.64, 2.27) * mm});
            skArc(sketch, "E683.filletArc", {"start": v(7.06, 3.69) * mm, "mid": v(6.47, 2.27) * mm, "end": v(7.06, 0.86) * mm});
            skPoint(sketch, "E684.visualSharp", {"position": v(-0.02, 7.93) * mm});
            skArc(sketch, "E684.filletArc", {"start": v(-1.43, 9.34) * mm, "mid": v(-0.02, 8.76) * mm, "end": v(1.4, 9.34) * mm});
            skLineSegment(sketch, "E685", {"start": v(-12.93, 15.17) * mm, "end": v(-11.16, 16.94) * mm, "construction": true});
            skLineSegment(sketch, "E686", {"start": v(-12.93, 15.17) * mm, "end": v(-14.7, 13.4) * mm, "construction": true});
            skLineSegment(sketch, "E687", {"start": v(-14.7, 13.4) * mm, "end": v(-27.43, 26.13) * mm, "construction": true});
            skPoint(sketch, "E688", {"position": v(-17.59, 16.3) * mm});
            skCircle(sketch, "E689", {"center": v(-15.28, 17.52) * mm, "radius": 4.62 * mm, "construction": true});
            skLineSegment(sketch, "E690", {"start": v(-27.43, 26.13) * mm, "end": v(-21.13, 10.9) * mm, "construction": true});
            skLineSegment(sketch, "E691", {"start": v(-15.28, 17.52) * mm, "end": v(-21.35, 11.45) * mm, "construction": true});
            skLineSegment(sketch, "E692", {"start": v(-18.88, 13.92) * mm, "end": v(-19.76, 13.03) * mm});
            skLineSegment(sketch, "E693", {"start": v(-22.2, 13.52) * mm, "end": v(-25.5, 21.5) * mm});
            skLineSegment(sketch, "E694", {"start": v(-23.88, 22.58) * mm, "end": v(-20.07, 18.78) * mm});
            skLineSegment(sketch, "E695", {"start": v(-19.86, 18.13) * mm, "end": v(-19.88, 18.01) * mm});
            skLineSegment(sketch, "E696", {"start": v(-18.86, 14.6) * mm, "end": v(-18.88, 14.62) * mm});
            skPoint(sketch, "E697", {"position": v(-19.7, 16.17) * mm});
            skArc(sketch, "E698", {"start": v(-19.88, 18.01) * mm, "mid": v(-19.72, 16.22) * mm, "end": v(-18.88, 14.62) * mm});
            skPoint(sketch, "E699.visualSharp", {"position": v(-27.43, 26.13) * mm});
            skArc(sketch, "E699.filletArc", {"start": v(-23.88, 22.58) * mm, "mid": v(-25.14, 22.7) * mm, "end": v(-25.5, 21.5) * mm});
            skPoint(sketch, "E700.visualSharp", {"position": v(-21.35, 11.45) * mm});
            skArc(sketch, "E700.filletArc", {"start": v(-22.2, 13.52) * mm, "mid": v(-21.12, 12.62) * mm, "end": v(-19.76, 13.03) * mm});
            skPoint(sketch, "E701.visualSharp", {"position": v(-18.55, 14.25) * mm});
            skArc(sketch, "E701.filletArc", {"start": v(-18.88, 13.92) * mm, "mid": v(-18.74, 14.26) * mm, "end": v(-18.86, 14.6) * mm});
            skPoint(sketch, "E702.visualSharp", {"position": v(-19.8, 18.5) * mm});
            skArc(sketch, "E702.filletArc", {"start": v(-19.86, 18.13) * mm, "mid": v(-19.89, 18.48) * mm, "end": v(-20.07, 18.78) * mm});
            skCircle(sketch, "E703", {"center": v(15.22, 17.54) * mm, "radius": 4.62 * mm, "construction": true});
            skLineSegment(sketch, "E704", {"start": v(15.22, 17.54) * mm, "end": v(12.89, 15.18) * mm, "construction": true});
            skLineSegment(sketch, "E705", {"start": v(12.89, 15.18) * mm, "end": v(14.67, 13.42) * mm, "construction": true});
            skLineSegment(sketch, "E706", {"start": v(12.89, 15.18) * mm, "end": v(11.1, 16.93) * mm, "construction": true});
            skLineSegment(sketch, "E707", {"start": v(11.1, 16.93) * mm, "end": v(23.84, 29.66) * mm, "construction": true});
            skLineSegment(sketch, "E708", {"start": v(14.67, 13.42) * mm, "end": v(27.3, 26.24) * mm, "construction": true});
            skLineSegment(sketch, "E709", {"start": v(15.22, 17.52) * mm, "end": v(21.34, 11.5) * mm, "construction": true});
            skLineSegment(sketch, "E710", {"start": v(21.34, 11.5) * mm, "end": v(27.3, 26.24) * mm, "construction": true});
            skLineSegment(sketch, "E711", {"start": v(19.8, 18.17) * mm, "end": v(19.81, 18.06) * mm});
            skLineSegment(sketch, "E712", {"start": v(18.82, 14.64) * mm, "end": v(18.84, 14.66) * mm});
            skLineSegment(sketch, "E713", {"start": v(20, 18.83) * mm, "end": v(23.79, 22.67) * mm});
            skLineSegment(sketch, "E714", {"start": v(25.43, 21.6) * mm, "end": v(22.18, 13.58) * mm});
            skLineSegment(sketch, "E715", {"start": v(19.74, 13.07) * mm, "end": v(18.84, 13.95) * mm});
            skPoint(sketch, "E716", {"position": v(19.64, 16.2) * mm});
            skArc(sketch, "E717", {"start": v(18.84, 14.66) * mm, "mid": v(19.66, 16.26) * mm, "end": v(19.81, 18.06) * mm});
            skPoint(sketch, "E718.visualSharp", {"position": v(18.5, 14.29) * mm});
            skArc(sketch, "E718.filletArc", {"start": v(18.82, 14.64) * mm, "mid": v(18.7, 14.3) * mm, "end": v(18.84, 13.95) * mm});
            skPoint(sketch, "E719.visualSharp", {"position": v(19.73, 18.55) * mm});
            skArc(sketch, "E719.filletArc", {"start": v(20, 18.83) * mm, "mid": v(19.82, 18.52) * mm, "end": v(19.8, 18.17) * mm});
            skPoint(sketch, "E720.visualSharp", {"position": v(27.3, 26.24) * mm});
            skArc(sketch, "E720.filletArc", {"start": v(25.43, 21.6) * mm, "mid": v(25.05, 22.8) * mm, "end": v(23.79, 22.67) * mm});
            skPoint(sketch, "E721.visualSharp", {"position": v(21.34, 11.5) * mm});
            skArc(sketch, "E721.filletArc", {"start": v(19.74, 13.07) * mm, "mid": v(21.1, 12.67) * mm, "end": v(22.18, 13.58) * mm});
            skCircle(sketch, "E722", {"center": v(-15.25, -12.98) * mm, "radius": 4.62 * mm, "construction": true});
            skCircle(sketch, "E723", {"center": v(15.25, -12.98) * mm, "radius": 4.62 * mm, "construction": true});
            skLineSegment(sketch, "E724", {"start": v(-15.25, -12.98) * mm, "end": v(-12.9, -10.63) * mm, "construction": true});
            skLineSegment(sketch, "E725", {"start": v(-12.9, -10.63) * mm, "end": v(-11.14, -12.4) * mm, "construction": true});
            skLineSegment(sketch, "E726", {"start": v(-12.9, -10.63) * mm, "end": v(-14.67, -8.87) * mm, "construction": true});
            skLineSegment(sketch, "E727", {"start": v(-11.14, -12.4) * mm, "end": v(-23.86, -25.13) * mm, "construction": true});
            skLineSegment(sketch, "E728", {"start": v(-14.67, -8.87) * mm, "end": v(-27.4, -21.6) * mm, "construction": true});
            skLineSegment(sketch, "E729", {"start": v(-15.25, -12.98) * mm, "end": v(-9.17, -19.05) * mm, "construction": true});
            skLineSegment(sketch, "E730", {"start": v(-15.25, -12.98) * mm, "end": v(-21.32, -6.9) * mm, "construction": true});
            skLineSegment(sketch, "E731", {"start": v(-25.48, -16.95) * mm, "end": v(-22.18, -8.98) * mm});
            skLineSegment(sketch, "E732", {"start": v(-19.73, -8.5) * mm, "end": v(-18.85, -9.37) * mm});
            skLineSegment(sketch, "E733", {"start": v(-23.85, -18.04) * mm, "end": v(-20.04, -14.23) * mm});
            skLineSegment(sketch, "E734", {"start": v(-18.83, -10.06) * mm, "end": v(-18.85, -10.08) * mm});
            skLineSegment(sketch, "E735", {"start": v(-19.83, -13.58) * mm, "end": v(-19.85, -13.47) * mm});
            skPoint(sketch, "E736", {"position": v(-19.68, -11.67) * mm});
            skArc(sketch, "E737", {"start": v(-18.85, -10.08) * mm, "mid": v(-19.68, -11.67) * mm, "end": v(-19.85, -13.47) * mm});
            skPoint(sketch, "E738.visualSharp", {"position": v(-18.52, -9.7) * mm});
            skArc(sketch, "E738.filletArc", {"start": v(-18.83, -10.06) * mm, "mid": v(-18.7, -9.71) * mm, "end": v(-18.85, -9.37) * mm});
            skPoint(sketch, "E739.visualSharp", {"position": v(-19.77, -13.96) * mm});
            skArc(sketch, "E739.filletArc", {"start": v(-20.04, -14.23) * mm, "mid": v(-19.85, -13.93) * mm, "end": v(-19.83, -13.58) * mm});
            skPoint(sketch, "E740.visualSharp", {"position": v(-27.4, -21.6) * mm});
            skArc(sketch, "E740.filletArc", {"start": v(-25.48, -16.95) * mm, "mid": v(-25.11, -18.17) * mm, "end": v(-23.85, -18.04) * mm});
            skPoint(sketch, "E741.visualSharp", {"position": v(-21.32, -6.9) * mm});
            skArc(sketch, "E741.filletArc", {"start": v(-19.73, -8.5) * mm, "mid": v(-21.09, -8.08) * mm, "end": v(-22.18, -8.98) * mm});
            skLineSegment(sketch, "E742", {"start": v(15.25, -12.98) * mm, "end": v(12.9, -10.63) * mm, "construction": true});
            skLineSegment(sketch, "E743", {"start": v(12.9, -10.63) * mm, "end": v(14.68, -8.87) * mm, "construction": true});
            skLineSegment(sketch, "E744", {"start": v(12.9, -10.63) * mm, "end": v(11.14, -12.4) * mm, "construction": true});
            skLineSegment(sketch, "E745", {"start": v(14.68, -8.87) * mm, "end": v(27.4, -21.59) * mm, "construction": true});
            skLineSegment(sketch, "E746", {"start": v(15.25, -12.98) * mm, "end": v(21.32, -6.9) * mm, "construction": true});
            skLineSegment(sketch, "E747", {"start": v(22.18, -8.97) * mm, "end": v(25.49, -16.95) * mm});
            skLineSegment(sketch, "E748", {"start": v(23.86, -18.04) * mm, "end": v(20.04, -14.23) * mm});
            skLineSegment(sketch, "E749", {"start": v(19.74, -8.49) * mm, "end": v(18.86, -9.37) * mm});
            skLineSegment(sketch, "E750", {"start": v(18.84, -10.06) * mm, "end": v(18.86, -10.08) * mm});
            skLineSegment(sketch, "E751", {"start": v(19.83, -13.58) * mm, "end": v(19.85, -13.46) * mm});
            skPoint(sketch, "E752", {"position": v(19.64, -11.53) * mm});
            skArc(sketch, "E753", {"start": v(19.85, -13.46) * mm, "mid": v(19.69, -11.67) * mm, "end": v(18.86, -10.08) * mm});
            skPoint(sketch, "E754.visualSharp", {"position": v(21.32, -6.9) * mm});
            skArc(sketch, "E754.filletArc", {"start": v(22.18, -8.97) * mm, "mid": v(21.1, -8.08) * mm, "end": v(19.74, -8.49) * mm});
            skPoint(sketch, "E755.visualSharp", {"position": v(19.77, -13.96) * mm});
            skArc(sketch, "E755.filletArc", {"start": v(19.83, -13.58) * mm, "mid": v(19.86, -13.93) * mm, "end": v(20.04, -14.23) * mm});
            skPoint(sketch, "E756.visualSharp", {"position": v(18.52, -9.7) * mm});
            skArc(sketch, "E756.filletArc", {"start": v(18.86, -9.37) * mm, "mid": v(18.71, -9.7) * mm, "end": v(18.84, -10.06) * mm});
            skPoint(sketch, "E757.visualSharp", {"position": v(27.4, -21.59) * mm});
            skArc(sketch, "E757.filletArc", {"start": v(23.86, -18.04) * mm, "mid": v(25.12, -18.16) * mm, "end": v(25.49, -16.95) * mm});
            skLineSegment(sketch, "E758", {"start": v(-0.01, -29.14) * mm, "end": v(15.24, -29.14) * mm, "construction": true});
            skPoint(sketch, "E759.visualSharp", {"position": v(-9.17, -19.05) * mm});
            skPoint(sketch, "E760.visualSharp", {"position": v(-11.98, -16.25) * mm});
            skPoint(sketch, "E761.visualSharp", {"position": v(-16.23, -17.5) * mm});
            skPoint(sketch, "E762.visualSharp", {"position": v(-23.86, -25.13) * mm});
            skLineSegment(sketch, "E763", {"start": v(15.25, -12.98) * mm, "end": v(9.18, -19.05) * mm, "construction": true});
            skLineSegment(sketch, "E764", {"start": v(11.14, -12.4) * mm, "end": v(23.88, -25.12) * mm, "construction": true});
            skPoint(sketch, "E765", {"position": v(13.76, -17.36) * mm});
            skPoint(sketch, "E766.visualSharp", {"position": v(9.18, -19.05) * mm});
            skPoint(sketch, "E767.visualSharp", {"position": v(11.98, -16.25) * mm});
            skPoint(sketch, "E768.visualSharp", {"position": v(23.88, -25.12) * mm});
            skPoint(sketch, "E769.visualSharp", {"position": v(16.24, -17.5) * mm});
            skPoint(sketch, "E770", {"position": v(-14.29, -17.5) * mm});
            skLineSegment(sketch, "E771", {"start": v(-28.67, 37.26) * mm, "end": v(-26.94, 36.26) * mm, "construction": true});
            skLineSegment(sketch, "E772", {"start": v(28.62, 37.26) * mm, "end": v(26.9, 36.24) * mm, "construction": true});
            skPoint(sketch, "E773", {"position": v(27.69, 36.82) * mm});
            skArc(sketch, "E774", {"start": v(28.62, 37.26) * mm, "mid": v(27.7, 36.84) * mm, "end": v(26.9, 36.24) * mm});
            skPoint(sketch, "E775", {"position": v(-27.73, 36.83) * mm});
            skArc(sketch, "E776", {"start": v(-26.94, 36.26) * mm, "mid": v(-27.76, 36.85) * mm, "end": v(-28.67, 37.26) * mm});
            skLineSegment(sketch, "E777", {"start": v(-26.94, 36.26) * mm, "end": v(-15.28, 26.77) * mm});
            skLineSegment(sketch, "E778", {"start": v(26.9, 36.24) * mm, "end": v(15.22, 26.77) * mm});
            skPoint(sketch, "E779", {"position": v(-0.03, 22) * mm});
            skFitSpline(sketch, "E780", {"points": [v(-15.28, 26.77) * mm, v(-0.03, 22) * mm, v(15.22, 26.77) * mm], "startDerivative": vector(26.4, -17.68) * mm, "endDerivative": vector(26.05, 17.77) * mm});
            skLineSegment(sketch, "E781", {"start": v(10.88, 23.81) * mm, "end": v(0, 23.82) * mm, "construction": true});
            skLineSegment(sketch, "E782", {"start": v(0, 23.82) * mm, "end": v(-10.88, 23.83) * mm, "construction": true});
            skLineSegment(sketch, "E783", {"start": v(-28.65, -32.7) * mm, "end": v(-26.92, -31.7) * mm, "construction": true});
            skLineSegment(sketch, "E784", {"start": v(28.64, -32.72) * mm, "end": v(26.91, -31.71) * mm, "construction": true});
            skPoint(sketch, "E785", {"position": v(27.67, -32.27) * mm});
            skArc(sketch, "E786", {"start": v(26.91, -31.71) * mm, "mid": v(27.73, -32.3) * mm, "end": v(28.64, -32.72) * mm});
            skPoint(sketch, "E787", {"position": v(-27.7, -32.27) * mm});
            skArc(sketch, "E788", {"start": v(-28.65, -32.7) * mm, "mid": v(-27.73, -32.29) * mm, "end": v(-26.92, -31.7) * mm});
            skLineSegment(sketch, "E789", {"start": v(-0.01, -29.14) * mm, "end": v(-15.26, -29.14) * mm, "construction": true});
            skLineSegment(sketch, "E790", {"start": v(-26.92, -31.7) * mm, "end": v(-15.26, -23.98) * mm});
            skLineSegment(sketch, "E791", {"start": v(26.91, -31.71) * mm, "end": v(15.24, -23.98) * mm});
            skLineSegment(sketch, "E792", {"start": v(-0.01, -14.83) * mm, "end": v(-0.01, -17.45) * mm, "construction": true});
            skLineSegment(sketch, "E793", {"start": v(-0.01, -17.45) * mm, "end": v(-0.01, -19.27) * mm, "construction": true});
            skFitSpline(sketch, "E794", {"points": [v(-15.26, -23.98) * mm, v(-0.01, -17.45) * mm, v(15.24, -23.98) * mm], "startDerivative": vector(30.5, 19.6) * mm, "endDerivative": vector(30.5, -19.6) * mm});
            skLineSegment(sketch, "E795", {"start": v(-0.01, -19.27) * mm, "end": v(10.87, -19.27) * mm, "construction": true});
            skLineSegment(sketch, "E796", {"start": v(-0.01, -19.27) * mm, "end": v(-10.9, -19.27) * mm, "construction": true});
            skLineSegment(sketch, "E797", {"start": v(0, -12.98) * mm, "end": v(0, -10.98) * mm, "construction": true});
            skFitSpline(sketch, "E798", {"points": [v(-7.75, -12.98) * mm, v(0, -10.98) * mm, v(7.72, -12.98) * mm], "startDerivative": vector(15.5, 6) * mm, "endDerivative": vector(15.45, -6) * mm});
            skLineSegment(sketch, "E799", {"start": v(-0.03, 17.52) * mm, "end": v(-0.03, 15.52) * mm, "construction": true});
            skFitSpline(sketch, "E800", {"points": [v(-7.75, 17.52) * mm, v(-0.03, 15.52) * mm, v(7.72, 17.52) * mm], "startDerivative": vector(15.45, -6) * mm, "endDerivative": vector(15.5, 6) * mm});
            skSolve(sketch);
        }
        {
            var Q0;
            Q0=qCreatedBy(makeId("Top.planeOp"),FACE);
            var sketch = newSketch(context, id + "F6", { "sketchPlane" : qUnion([Q0])});
            skLineSegment(sketch, "E801.bottom", {"start": v(-15.25, 15.28) * mm, "end": v(15.25, 15.28) * mm, "construction": true});
            skLineSegment(sketch, "E801.top", {"start": v(-15.25, -15.22) * mm, "end": v(15.25, -15.22) * mm, "construction": true});
            skLineSegment(sketch, "E801.left", {"start": v(-15.25, 15.28) * mm, "end": v(-15.25, -15.22) * mm, "construction": true});
            skLineSegment(sketch, "E801.right", {"start": v(15.25, 15.28) * mm, "end": v(15.25, -15.22) * mm, "construction": true});
            skPoint(sketch, "E801.middle", {"position": v(0, 0.03) * mm});
            skLineSegment(sketch, "E802.bottom", {"start": v(30.25, 30.28) * mm, "end": v(-30.25, 30.28) * mm, "construction": true});
            skLineSegment(sketch, "E802.top", {"start": v(30.25, -30.22) * mm, "end": v(-30.25, -30.22) * mm, "construction": true});
            skLineSegment(sketch, "E802.left", {"start": v(30.25, 30.28) * mm, "end": v(30.25, -30.22) * mm, "construction": true});
            skLineSegment(sketch, "E802.right", {"start": v(-30.25, 30.28) * mm, "end": v(-30.25, -30.22) * mm, "construction": true});
            skLineSegment(sketch, "E803.bottom", {"start": v(-70.96, 70.99) * mm, "end": v(70.96, 70.99) * mm, "construction": true});
            skLineSegment(sketch, "E803.top", {"start": v(-70.96, -70.93) * mm, "end": v(70.96, -70.93) * mm, "construction": true});
            skLineSegment(sketch, "E803.left", {"start": v(-70.96, 70.99) * mm, "end": v(-70.96, -70.93) * mm, "construction": true});
            skLineSegment(sketch, "E803.right", {"start": v(70.96, 70.99) * mm, "end": v(70.96, -70.93) * mm, "construction": true});
            skCircle(sketch, "E804", {"center": v(70.96, 70.99) * mm, "radius": 4.5 * mm, "construction": true});
            skCircle(sketch, "E805", {"center": v(-70.96, 70.99) * mm, "radius": 4.5 * mm, "construction": true});
            skCircle(sketch, "E806", {"center": v(70.96, -70.93) * mm, "radius": 4.5 * mm, "construction": true});
            skCircle(sketch, "E807", {"center": v(-70.96, -70.93) * mm, "radius": 4.5 * mm, "construction": true});
            skCircle(sketch, "E808", {"center": v(70.96, 70.99) * mm, "radius": 8 * mm, "construction": true});
            skCircle(sketch, "E809", {"center": v(70.96, -70.93) * mm, "radius": 8 * mm, "construction": true});
            skCircle(sketch, "E810", {"center": v(-70.96, -70.93) * mm, "radius": 8 * mm, "construction": true});
            skCircle(sketch, "E811", {"center": v(-70.96, 70.99) * mm, "radius": 8 * mm, "construction": true});
            skCircle(sketch, "E812", {"center": v(70.96, 70.99) * mm, "radius": 9.5 * mm, "construction": true});
            skCircle(sketch, "E813", {"center": v(70.96, -70.93) * mm, "radius": 9.5 * mm, "construction": true});
            skCircle(sketch, "E814", {"center": v(-70.96, -70.93) * mm, "radius": 9.5 * mm, "construction": true});
            skCircle(sketch, "E815", {"center": v(-70.96, 70.99) * mm, "radius": 9.5 * mm, "construction": true});
            skCircle(sketch, "E816", {"center": v(70.96, 70.99) * mm, "radius": 14 * mm, "construction": true});
            skCircle(sketch, "E817", {"center": v(-70.96, 70.99) * mm, "radius": 14 * mm, "construction": true});
            skCircle(sketch, "E818", {"center": v(70.96, -70.93) * mm, "radius": 14 * mm, "construction": true});
            skCircle(sketch, "E819", {"center": v(-70.96, -70.93) * mm, "radius": 14 * mm, "construction": true});
            skCircle(sketch, "E820", {"center": v(70.96, 70.99) * mm, "radius": 63.5 * mm, "construction": true});
            skCircle(sketch, "E821", {"center": v(70.96, -70.93) * mm, "radius": 63.5 * mm, "construction": true});
            skCircle(sketch, "E822", {"center": v(-70.96, -70.93) * mm, "radius": 63.5 * mm, "construction": true});
            skCircle(sketch, "E823", {"center": v(-70.96, 70.99) * mm, "radius": 63.5 * mm, "construction": true});
            skLineSegment(sketch, "E824", {"start": v(0, 30.28) * mm, "end": v(0, 33.77) * mm, "construction": true});
            skLineSegment(sketch, "E825", {"start": v(0, -30.22) * mm, "end": v(0, -33.72) * mm, "construction": true});
            skLineSegment(sketch, "E826", {"start": v(0, -33.72) * mm, "end": v(-15, -33.72) * mm, "construction": true});
            skLineSegment(sketch, "E827", {"start": v(0, -33.72) * mm, "end": v(15, -33.72) * mm, "construction": true});
            skLineSegment(sketch, "E828.bottom", {"start": v(-26.19, 26.22) * mm, "end": v(26.2, 26.22) * mm, "construction": true});
            skLineSegment(sketch, "E828.top", {"start": v(-26.19, -26.16) * mm, "end": v(26.2, -26.16) * mm, "construction": true});
            skLineSegment(sketch, "E828.left", {"start": v(-26.19, 26.22) * mm, "end": v(-26.19, -26.16) * mm, "construction": true});
            skLineSegment(sketch, "E828.right", {"start": v(26.2, 26.22) * mm, "end": v(26.2, -26.16) * mm, "construction": true});
            skCircle(sketch, "E829", {"center": v(30.25, 30.28) * mm, "radius": 3.57 * mm, "construction": true});
            skCircle(sketch, "E830", {"center": v(-30.25, 30.28) * mm, "radius": 3.57 * mm, "construction": true});
            skCircle(sketch, "E831", {"center": v(30.25, -30.22) * mm, "radius": 3.57 * mm, "construction": true});
            skCircle(sketch, "E832", {"center": v(-30.25, -30.22) * mm, "radius": 3.57 * mm, "construction": true});
            skLineSegment(sketch, "E833", {"start": v(-70.96, 70.99) * mm, "end": v(70.96, -70.93) * mm, "construction": true});
            skLineSegment(sketch, "E834", {"start": v(0, -26.16) * mm, "end": v(17.54, -26.16) * mm, "construction": true});
            skLineSegment(sketch, "E835", {"start": v(0, -26.16) * mm, "end": v(-17.54, -26.16) * mm, "construction": true});
            skLineSegment(sketch, "E836", {"start": v(0, -33.72) * mm, "end": v(0, -44.57) * mm, "construction": true});
            skLineSegment(sketch, "E837", {"start": v(0, -44.57) * mm, "end": v(0, -48.1) * mm, "construction": true});
            skLineSegment(sketch, "E838", {"start": v(0, -44.57) * mm, "end": v(11, -44.57) * mm, "construction": true});
            skLineSegment(sketch, "E839", {"start": v(0, -44.57) * mm, "end": v(-11, -44.57) * mm, "construction": true});
            skLineSegment(sketch, "E840", {"start": v(-15.25, -15.22) * mm, "end": v(-19.25, -15.22) * mm, "construction": true});
            skLineSegment(sketch, "E841", {"start": v(15.25, -15.22) * mm, "end": v(19.25, -15.22) * mm, "construction": true});
            skLineSegment(sketch, "E842", {"start": v(15.25, 15.28) * mm, "end": v(19.25, 15.28) * mm, "construction": true});
            skLineSegment(sketch, "E843", {"start": v(-15.25, 15.28) * mm, "end": v(-19.25, 15.28) * mm, "construction": true});
            skLineSegment(sketch, "E844", {"start": v(-16.22, -31.94) * mm, "end": v(0, -31.94) * mm, "construction": true});
            skLineSegment(sketch, "E845", {"start": v(0, -31.94) * mm, "end": v(16.22, -31.94) * mm, "construction": true});
            skLineSegment(sketch, "E846", {"start": v(-12.6, -42.84) * mm, "end": v(0, -42.84) * mm, "construction": true});
            skLineSegment(sketch, "E847", {"start": v(0, -42.84) * mm, "end": v(12.6, -42.84) * mm, "construction": true});
            skFitSpline(sketch, "E848", {"points": [v(-11, -44.57) * mm, v(0, -48.1) * mm], "startDerivative": vector(9.3, -7.23) * mm, "endDerivative": vector(12, -2.3) * mm});
            skFitSpline(sketch, "E849", {"points": [v(11, -44.57) * mm, v(0, -48.1) * mm], "startDerivative": vector(-9.3, -7.23) * mm, "endDerivative": vector(-12, -2.3) * mm});
            skLineSegment(sketch, "E850", {"start": v(-7.9, -46.98) * mm, "end": v(0, -46.98) * mm, "construction": true});
            skLineSegment(sketch, "E851", {"start": v(0, -46.98) * mm, "end": v(7.9, -46.98) * mm, "construction": true});
            skLineSegment(sketch, "E852", {"start": v(-4, -47.35) * mm, "end": v(0, -47.35) * mm, "construction": true});
            skLineSegment(sketch, "E853", {"start": v(0, -47.35) * mm, "end": v(4, -47.35) * mm, "construction": true});
            skCircle(sketch, "E854", {"center": v(-8.33, -41.13) * mm, "radius": 1.5 * mm});
            skCircle(sketch, "E855", {"center": v(8.33, -41.13) * mm, "radius": 1.5 * mm});
            skFitSpline(sketch, "E856", {"points": [v(-15, 33.77) * mm, v(-19.25, 15.28) * mm], "startDerivative": vector(-1.66, -47.23) * mm, "endDerivative": vector(-4.95, -22.5) * mm});
            skFitSpline(sketch, "E857", {"points": [v(15, 33.77) * mm, v(19.25, 15.28) * mm], "startDerivative": vector(1.66, -47.23) * mm, "endDerivative": vector(4.95, -22.5) * mm});
            skLineSegment(sketch, "E858", {"start": v(-19.25, 15.28) * mm, "end": v(-19.25, -15.22) * mm});
            skLineSegment(sketch, "E859", {"start": v(19.25, 15.28) * mm, "end": v(19.25, -15.22) * mm});
            skLineSegment(sketch, "E860", {"start": v(15.55, 18.03) * mm, "end": v(0, 18.03) * mm, "construction": true});
            skLineSegment(sketch, "E861", {"start": v(0, 18.03) * mm, "end": v(-15.55, 18.03) * mm, "construction": true});
            skPoint(sketch, "E862.visualSharp", {"position": v(-17.54, -26.16) * mm});
            skPoint(sketch, "E863.visualSharp", {"position": v(17.54, -26.16) * mm});
            skFitSpline(sketch, "E864", {"points": [v(-19.25, -15.22) * mm, v(-17.54, -26.16) * mm, v(-12.6, -42.84) * mm, v(-11, -44.57) * mm], "startDerivative": vector(1.48, -36.7) * mm, "endDerivative": vector(10.67, -6.67) * mm});
            skFitSpline(sketch, "E865", {"points": [v(19.25, -15.22) * mm, v(17.54, -26.16) * mm, v(12.6, -42.84) * mm, v(11, -44.57) * mm], "startDerivative": vector(-1.5, -36.7) * mm, "endDerivative": vector(-10.67, -6.67) * mm});
            skLineSegment(sketch, "E866", {"start": v(-8.33, -41.13) * mm, "end": v(-13.33, -41.13) * mm, "construction": true});
            skLineSegment(sketch, "E867", {"start": v(-8.33, -41.13) * mm, "end": v(-8.33, -46.13) * mm, "construction": true});
            skLineSegment(sketch, "E868", {"start": v(8.33, -41.13) * mm, "end": v(13.33, -41.13) * mm, "construction": true});
            skLineSegment(sketch, "E869", {"start": v(8.33, -41.13) * mm, "end": v(8.33, -46.13) * mm, "construction": true});
            skCircle(sketch, "E870", {"center": v(11.5, 39.06) * mm, "radius": 1.5 * mm});
            skCircle(sketch, "E871", {"center": v(-15.25, 15.28) * mm, "radius": 1.5 * mm});
            skCircle(sketch, "E872", {"center": v(15.25, 15.28) * mm, "radius": 1.5 * mm});
            skCircle(sketch, "E873", {"center": v(15.25, -15.22) * mm, "radius": 1.5 * mm});
            skCircle(sketch, "E874", {"center": v(-15.25, -15.22) * mm, "radius": 1.5 * mm});
            skLineSegment(sketch, "E875.bottom", {"start": v(-13.67, 13.7) * mm, "end": v(13.68, 13.7) * mm, "construction": true});
            skLineSegment(sketch, "E875.top", {"start": v(-13.67, -13.65) * mm, "end": v(13.68, -13.65) * mm, "construction": true});
            skLineSegment(sketch, "E875.left", {"start": v(-13.68, 13.7) * mm, "end": v(-13.68, -13.65) * mm, "construction": true});
            skLineSegment(sketch, "E875.right", {"start": v(13.67, 13.7) * mm, "end": v(13.67, -13.65) * mm, "construction": true});
            skLineSegment(sketch, "E876.bottom", {"start": v(-4.75, 4.78) * mm, "end": v(4.75, 4.78) * mm, "construction": true});
            skLineSegment(sketch, "E876.top", {"start": v(-4.75, -4.72) * mm, "end": v(4.75, -4.72) * mm, "construction": true});
            skLineSegment(sketch, "E876.left", {"start": v(-4.75, 4.78) * mm, "end": v(-4.75, -4.72) * mm, "construction": true});
            skLineSegment(sketch, "E876.right", {"start": v(4.75, 4.78) * mm, "end": v(4.75, -4.72) * mm, "construction": true});
            skPoint(sketch, "E877", {"position": v(-4.75, 0.03) * mm});
            skPoint(sketch, "E878", {"position": v(0, 4.78) * mm});
            skPoint(sketch, "E879", {"position": v(4.75, 0.03) * mm});
            skPoint(sketch, "E880", {"position": v(0, -4.72) * mm});
            skLineSegment(sketch, "E881", {"start": v(-6.16, 1.44) * mm, "end": v(-11.97, 7.25) * mm});
            skLineSegment(sketch, "E882", {"start": v(-6.16, -1.39) * mm, "end": v(-11.97, -7.19) * mm});
            skLineSegment(sketch, "E883", {"start": v(-13.68, -6.48) * mm, "end": v(-13.68, 6.54) * mm});
            skLineSegment(sketch, "E884", {"start": v(6.16, -1.39) * mm, "end": v(11.97, -7.19) * mm});
            skLineSegment(sketch, "E885", {"start": v(6.16, 1.44) * mm, "end": v(11.97, 7.25) * mm});
            skLineSegment(sketch, "E886", {"start": v(13.67, 6.54) * mm, "end": v(13.67, -6.48) * mm});
            skArc(sketch, "E887.filletArc", {"start": v(-6.16, -1.39) * mm, "mid": v(-5.58, 0.03) * mm, "end": v(-6.16, 1.44) * mm});
            skPoint(sketch, "E888.visualSharp", {"position": v(-13.67, 8.95) * mm});
            skArc(sketch, "E888.filletArc", {"start": v(-11.97, 7.25) * mm, "mid": v(-13.06, 7.46) * mm, "end": v(-13.67, 6.54) * mm});
            skPoint(sketch, "E889.visualSharp", {"position": v(-13.67, -8.9) * mm});
            skArc(sketch, "E889.filletArc", {"start": v(-13.67, -6.48) * mm, "mid": v(-13.06, -7.4) * mm, "end": v(-11.97, -7.19) * mm});
            skArc(sketch, "E890.filletArc", {"start": v(6.16, 1.44) * mm, "mid": v(5.58, 0.03) * mm, "end": v(6.16, -1.39) * mm});
            skPoint(sketch, "E891.visualSharp", {"position": v(13.68, 8.95) * mm});
            skArc(sketch, "E891.filletArc", {"start": v(13.68, 6.54) * mm, "mid": v(13.06, 7.46) * mm, "end": v(11.97, 7.25) * mm});
            skPoint(sketch, "E892.visualSharp", {"position": v(13.68, -8.9) * mm});
            skArc(sketch, "E892.filletArc", {"start": v(11.97, -7.19) * mm, "mid": v(13.06, -7.4) * mm, "end": v(13.68, -6.48) * mm});
            skLineSegment(sketch, "E893", {"start": v(1.41, -6.14) * mm, "end": v(7.22, -11.94) * mm});
            skLineSegment(sketch, "E894", {"start": v(-1.41, -6.14) * mm, "end": v(-7.22, -11.94) * mm});
            skLineSegment(sketch, "E895", {"start": v(-6.51, -13.65) * mm, "end": v(6.51, -13.65) * mm});
            skArc(sketch, "E896.filletArc", {"start": v(1.41, -6.14) * mm, "mid": v(0, -5.55) * mm, "end": v(-1.41, -6.14) * mm});
            skPoint(sketch, "E897.visualSharp", {"position": v(8.92, -13.65) * mm});
            skArc(sketch, "E897.filletArc", {"start": v(6.51, -13.65) * mm, "mid": v(7.43, -13.03) * mm, "end": v(7.22, -11.94) * mm});
            skPoint(sketch, "E898.visualSharp", {"position": v(-8.93, -13.65) * mm});
            skArc(sketch, "E898.filletArc", {"start": v(-7.22, -11.94) * mm, "mid": v(-7.43, -13.03) * mm, "end": v(-6.51, -13.65) * mm});
            skLineSegment(sketch, "E899", {"start": v(0, -17.8) * mm, "end": v(13.36, -17.8) * mm, "construction": true});
            skPoint(sketch, "E900", {"position": v(0, -17.8) * mm});
            skLineSegment(sketch, "E901", {"start": v(0, -17.8) * mm, "end": v(-13.36, -17.8) * mm, "construction": true});
            skLineSegment(sketch, "E902", {"start": v(-8.92, -13.65) * mm, "end": v(-8.92, -17.8) * mm, "construction": true});
            skLineSegment(sketch, "E903", {"start": v(8.92, -13.65) * mm, "end": v(8.92, -17.8) * mm, "construction": true});
            skLineSegment(sketch, "E904", {"start": v(0, -17.8) * mm, "end": v(0, -26.72) * mm, "construction": true});
            skLineSegment(sketch, "E905", {"start": v(-7.22, -19.5) * mm, "end": v(-1.41, -25.3) * mm});
            skLineSegment(sketch, "E906", {"start": v(1.41, -25.3) * mm, "end": v(7.22, -19.5) * mm});
            skLineSegment(sketch, "E907", {"start": v(6.51, -17.8) * mm, "end": v(-6.51, -17.8) * mm});
            skPoint(sketch, "E908.visualSharp", {"position": v(-8.92, -17.8) * mm});
            skArc(sketch, "E908.filletArc", {"start": v(-6.51, -17.8) * mm, "mid": v(-7.43, -18.42) * mm, "end": v(-7.22, -19.5) * mm});
            skPoint(sketch, "E909.visualSharp", {"position": v(8.92, -17.8) * mm});
            skArc(sketch, "E909.filletArc", {"start": v(7.22, -19.5) * mm, "mid": v(7.43, -18.42) * mm, "end": v(6.51, -17.8) * mm});
            skPoint(sketch, "E910.visualSharp", {"position": v(0, -26.72) * mm});
            skArc(sketch, "E910.filletArc", {"start": v(-1.41, -25.3) * mm, "mid": v(0, -25.9) * mm, "end": v(1.41, -25.3) * mm});
            skLineSegment(sketch, "E911", {"start": v(0, -21.22) * mm, "end": v(-11.7, -21.22) * mm, "construction": true});
            skLineSegment(sketch, "E912", {"start": v(0, -21.22) * mm, "end": v(11.7, -21.22) * mm, "construction": true});
            skLineSegment(sketch, "E913", {"start": v(-10.43, -22.48) * mm, "end": v(-4.5, -28.4) * mm});
            skLineSegment(sketch, "E914", {"start": v(-3.92, -29.82) * mm, "end": v(-3.92, -33) * mm});
            skLineSegment(sketch, "E915", {"start": v(-11.27, -22.95) * mm, "end": v(-9.07, -31.94) * mm});
            skArc(sketch, "E916", {"start": v(-9.07, -31.94) * mm, "mid": v(-6.94, -34.19) * mm, "end": v(-3.92, -33.5) * mm, "construction": true});
            skLineSegment(sketch, "E917", {"start": v(-4.32, -33.8) * mm, "end": v(-4.4, -33.86) * mm});
            skPoint(sketch, "E918", {"position": v(-6.94, -34.19) * mm});
            skArc(sketch, "E919", {"start": v(-9.07, -31.94) * mm, "mid": v(-7.22, -34.09) * mm, "end": v(-4.4, -33.86) * mm});
            skPoint(sketch, "E920.visualSharp", {"position": v(-11.7, -21.22) * mm});
            skArc(sketch, "E920.filletArc", {"start": v(-10.43, -22.48) * mm, "mid": v(-11.03, -22.4) * mm, "end": v(-11.27, -22.95) * mm});
            skPoint(sketch, "E921.visualSharp", {"position": v(-3.92, -29) * mm});
            skArc(sketch, "E921.filletArc", {"start": v(-3.92, -29.82) * mm, "mid": v(-4.07, -29.06) * mm, "end": v(-4.5, -28.4) * mm});
            skPoint(sketch, "E922.visualSharp", {"position": v(-3.92, -33.5) * mm});
            skArc(sketch, "E922.filletArc", {"start": v(-4.32, -33.8) * mm, "mid": v(-4.03, -33.44) * mm, "end": v(-3.92, -33) * mm});
            skLineSegment(sketch, "E923", {"start": v(10.43, -22.48) * mm, "end": v(4.5, -28.4) * mm});
            skLineSegment(sketch, "E924", {"start": v(3.92, -29.82) * mm, "end": v(3.92, -33) * mm});
            skLineSegment(sketch, "E925", {"start": v(3.92, -31.94) * mm, "end": v(9.07, -31.94) * mm, "construction": true});
            skArc(sketch, "E926", {"start": v(3.92, -33.5) * mm, "mid": v(6.94, -34.19) * mm, "end": v(9.07, -31.94) * mm, "construction": true});
            skLineSegment(sketch, "E927", {"start": v(11.27, -22.95) * mm, "end": v(9.07, -31.94) * mm});
            skLineSegment(sketch, "E928", {"start": v(4.32, -33.8) * mm, "end": v(4.4, -33.86) * mm});
            skPoint(sketch, "E929", {"position": v(6.94, -34.19) * mm});
            skArc(sketch, "E930", {"start": v(4.4, -33.86) * mm, "mid": v(7.22, -34.09) * mm, "end": v(9.07, -31.94) * mm});
            skPoint(sketch, "E931.visualSharp", {"position": v(3.92, -29) * mm});
            skArc(sketch, "E931.filletArc", {"start": v(4.5, -28.4) * mm, "mid": v(4.07, -29.06) * mm, "end": v(3.92, -29.82) * mm});
            skPoint(sketch, "E932.visualSharp", {"position": v(3.92, -33.5) * mm});
            skArc(sketch, "E932.filletArc", {"start": v(3.92, -33) * mm, "mid": v(4.03, -33.44) * mm, "end": v(4.32, -33.8) * mm});
            skPoint(sketch, "E933.visualSharp", {"position": v(11.7, -21.22) * mm});
            skArc(sketch, "E933.filletArc", {"start": v(11.27, -22.95) * mm, "mid": v(11.03, -22.4) * mm, "end": v(10.43, -22.48) * mm});
            skLineSegment(sketch, "E934", {"start": v(-8.92, -13.65) * mm, "end": v(-8.92, 13.7) * mm, "construction": true});
            skLineSegment(sketch, "E935", {"start": v(8.92, -13.65) * mm, "end": v(8.92, 13.7) * mm, "construction": true});
            skLineSegment(sketch, "E936", {"start": v(-1.41, 6.2) * mm, "end": v(-7.22, 12) * mm});
            skLineSegment(sketch, "E937", {"start": v(1.41, 6.2) * mm, "end": v(7.22, 12) * mm});
            skLineSegment(sketch, "E938", {"start": v(6.51, 13.7) * mm, "end": v(-6.51, 13.7) * mm});
            skArc(sketch, "E939.filletArc", {"start": v(-1.41, 6.2) * mm, "mid": v(0, 5.6) * mm, "end": v(1.41, 6.2) * mm});
            skPoint(sketch, "E940.visualSharp", {"position": v(8.92, 13.7) * mm});
            skArc(sketch, "E940.filletArc", {"start": v(7.22, 12) * mm, "mid": v(7.43, 13.09) * mm, "end": v(6.51, 13.7) * mm});
            skPoint(sketch, "E941.visualSharp", {"position": v(-8.93, 13.7) * mm});
            skArc(sketch, "E941.filletArc", {"start": v(-6.51, 13.7) * mm, "mid": v(-7.43, 13.09) * mm, "end": v(-7.22, 12) * mm});
            skPoint(sketch, "E942.endSnap0", {"position": v(0, 32.03) * mm});
            skPoint(sketch, "E943.visualSharp", {"position": v(-8.73, 24.54) * mm});
            skPoint(sketch, "E944.visualSharp", {"position": v(8.73, 24.54) * mm});
            skCircle(sketch, "E945", {"center": v(-11.5, 39.06) * mm, "radius": 1.5 * mm});
            skLineSegment(sketch, "E946", {"start": v(-15.08, 38.9) * mm, "end": v(-15.08, 31.86) * mm});
            skLineSegment(sketch, "E947", {"start": v(15.08, 38.9) * mm, "end": v(15.08, 31.86) * mm});
            skPoint(sketch, "E948.visualSharp", {"position": v(-15.08, 43.2) * mm});
            skArc(sketch, "E948.filletArc", {"start": v(-10.78, 43.2) * mm, "mid": v(-13.82, 41.93) * mm, "end": v(-15.08, 38.9) * mm});
            skPoint(sketch, "E949.visualSharp", {"position": v(15.08, 43.2) * mm});
            skArc(sketch, "E949.filletArc", {"start": v(15.08, 38.9) * mm, "mid": v(13.82, 41.93) * mm, "end": v(10.78, 43.2) * mm});
            skLineSegment(sketch, "E950", {"start": v(-10.78, 43.2) * mm, "end": v(-7.28, 43.2) * mm});
            skLineSegment(sketch, "E951", {"start": v(10.78, 43.2) * mm, "end": v(7.28, 43.2) * mm});
            skLineSegment(sketch, "E952", {"start": v(-7.28, 43.2) * mm, "end": v(-7.28, 28.2) * mm});
            skLineSegment(sketch, "E953", {"start": v(-7.28, 28.2) * mm, "end": v(7.28, 28.2) * mm});
            skLineSegment(sketch, "E954", {"start": v(7.28, 28.2) * mm, "end": v(7.28, 43.2) * mm});
            skSolve(sketch);
        }
        {
            var Q0;
            Q0=qSketchRegion(id+"F6",true);
            extrude(context, id + "F7", {"entities" : qUnion([Q0]), "depth" : 21.5 * mm, "hasSecondDirection" : true, "secondDirectionOppositeDirection" : false, "secondDirectionDepth" : 20 * mm});
        }
        {
            var Q0;
            Q0=qSketchRegion(id+"F5",true);
            extrude(context, id + "F8", {"entities" : qUnion([Q0]), "depth" : 10.5 * mm, "hasSecondDirection" : true, "secondDirectionOppositeDirection" : false, "secondDirectionDepth" : 9 * mm});
        }
    });
